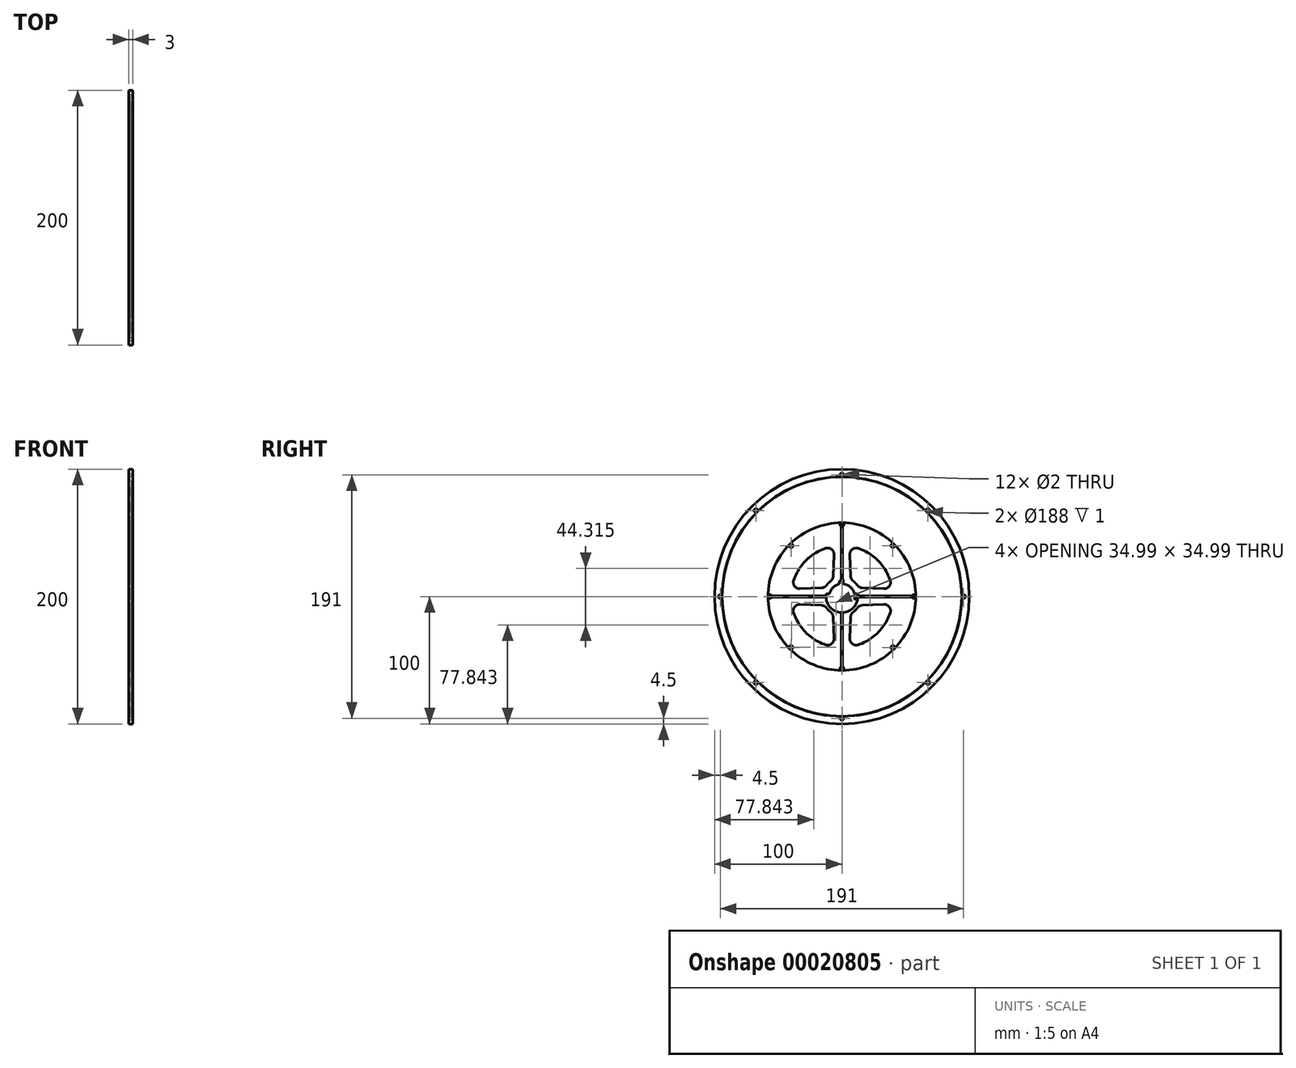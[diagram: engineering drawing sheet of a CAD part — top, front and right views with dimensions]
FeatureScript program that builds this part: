
annotation { "Feature Type Name" : "Feature", "Feature Type Description" : "" }
export const myFeature = defineFeature(function(context is Context, id is Id, definition is map)
    precondition{}
    {
        {
            var Q0;
            Q0=qCreatedBy(makeId("Right.planeOp"),FACE);
            var sketch = newSketch(context, id + "F0", { "sketchPlane" : qUnion([Q0])});
            skCircle(sketch, "E0", {"center": v(0, 0) * mm, "radius": 100 * mm});
            skCircle(sketch, "E1", {"center": v(0, 0) * mm, "radius": 97 * mm});
            skCircle(sketch, "E2", {"center": v(0, 0) * mm, "radius": 58 * mm});
            skCircle(sketch, "E3", {"center": v(0, 0) * mm, "radius": 40 * mm});
            skCircle(sketch, "E4", {"center": v(0, 0) * mm, "radius": 15 * mm});
            skCircle(sketch, "E5", {"center": v(0, 0) * mm, "radius": 10 * mm});
            skCircle(sketch, "E6", {"center": v(0, 0) * mm, "radius": 12.5 * mm});
            skCircle(sketch, "E7", {"center": v(0, 0) * mm, "radius": 55 * mm});
            skCircle(sketch, "E8", {"center": v(0, 0) * mm, "radius": 94 * mm});
            skLineSegment(sketch, "E9", {"start": v(-97, 0) * mm, "end": v(-94, 0) * mm});
            skLineSegment(sketch, "E10", {"start": v(-58, 0) * mm, "end": v(-55, 0) * mm});
            skLineSegment(sketch, "E11.rect.bottom", {"start": v(-55, -0.5) * mm, "end": v(55, -0.5) * mm});
            skLineSegment(sketch, "E11.rect.top", {"start": v(-55, 0.5) * mm, "end": v(55, 0.5) * mm});
            skLineSegment(sketch, "E11.rect.left", {"start": v(-55, -0.5) * mm, "end": v(-55, 0.5) * mm});
            skLineSegment(sketch, "E11.rect.right", {"start": v(55, -0.5) * mm, "end": v(55, 0.5) * mm});
            skEllipse(sketch, "E12", {"center": v(-55, 0) * mm, "majorRadius": 1.5 * mm, "minorRadius": 0.5 * mm, "majorAxis": v(-1, 0)});
            skEllipse(sketch, "E13.1.0", {"center": v(0, -55) * mm, "majorRadius": 1.5 * mm, "minorRadius": 0.5 * mm, "majorAxis": v(0, -1)});
            skEllipse(sketch, "E13.2.0", {"center": v(55, 0) * mm, "majorRadius": 1.5 * mm, "minorRadius": 0.5 * mm, "majorAxis": v(1, 0)});
            skEllipse(sketch, "E13.3.0", {"center": v(0, 55) * mm, "majorRadius": 1.5 * mm, "minorRadius": 0.5 * mm, "majorAxis": v(0, 1)});
            skLineSegment(sketch, "E14.rect.bottom", {"start": v(-0.5, 55) * mm, "end": v(0.5, 55) * mm});
            skLineSegment(sketch, "E14.rect.top", {"start": v(-0.5, -55) * mm, "end": v(0.5, -55) * mm});
            skLineSegment(sketch, "E14.rect.left", {"start": v(-0.5, 55) * mm, "end": v(-0.5, -55) * mm});
            skLineSegment(sketch, "E14.rect.right", {"start": v(0.5, 55) * mm, "end": v(0.5, -55) * mm});
            skCircle(sketch, "E15.cCircle", {"center": v(0, 0) * mm, "radius": 58 * mm, "construction": true});
            skPoint(sketch, "E16.0.midPoint", {"position": v(-58, 0) * mm});
            skLineSegment(sketch, "E17.rect.bottom", {"start": v(-2, 12.34) * mm, "end": v(2, 12.34) * mm});
            skLineSegment(sketch, "E17.rect.top", {"start": v(-2, -12.34) * mm, "end": v(2, -12.34) * mm});
            skLineSegment(sketch, "E17.rect.left", {"start": v(-2, 12.34) * mm, "end": v(-2, -12.34) * mm});
            skLineSegment(sketch, "E17.rect.right", {"start": v(2, 12.34) * mm, "end": v(2, -12.34) * mm});
            skLineSegment(sketch, "E18.rect.bottom", {"start": v(-12.34, -2) * mm, "end": v(12.34, -2) * mm});
            skLineSegment(sketch, "E18.rect.top", {"start": v(-12.34, 2) * mm, "end": v(12.34, 2) * mm});
            skLineSegment(sketch, "E18.rect.left", {"start": v(-12.34, -2) * mm, "end": v(-12.34, 2) * mm});
            skLineSegment(sketch, "E18.rect.right", {"start": v(12.34, -2) * mm, "end": v(12.34, 2) * mm});
            skCircle(sketch, "E19", {"center": v(12.5, 0) * mm, "radius": 0.5 * mm});
            skCircle(sketch, "E20", {"center": v(0, 12.5) * mm, "radius": 0.5 * mm});
            skCircle(sketch, "E21", {"center": v(-12.5, 0) * mm, "radius": 0.5 * mm});
            skCircle(sketch, "E22", {"center": v(0, -12.5) * mm, "radius": 0.5 * mm});
            skPoint(sketch, "E23.0.midPoint", {"position": v(58, 0) * mm});
            skLineSegment(sketch, "E24", {"start": v(5.87, 39.57) * mm, "end": v(7.02, 13.26) * mm});
            skLineSegment(sketch, "E25", {"start": v(-5.87, 39.57) * mm, "end": v(-7.02, 13.26) * mm});
            skLineSegment(sketch, "E26", {"start": v(5.87, -39.57) * mm, "end": v(7.02, -13.26) * mm});
            skLineSegment(sketch, "E27", {"start": v(-5.87, -39.57) * mm, "end": v(-7.02, -13.26) * mm});
            skLineSegment(sketch, "E28", {"start": v(-39.57, -5.87) * mm, "end": v(-13.26, -7.02) * mm});
            skLineSegment(sketch, "E29", {"start": v(-39.57, 5.87) * mm, "end": v(-13.26, 7.02) * mm});
            skLineSegment(sketch, "E30", {"start": v(39.57, 5.87) * mm, "end": v(13.26, 7.02) * mm});
            skLineSegment(sketch, "E31", {"start": v(39.57, -5.87) * mm, "end": v(13.26, -7.02) * mm});
            skSolve(sketch);
        }
        {
            var Q0;
            {var subQ0=sQuery(id+"F0.wireOp",EDGE,"E25");Q0=makeQuery(id+"F0.imprint","IMPRINT",FACE,{"disambiguationData":[TD([[makeQuery(id+"F0.imprint","IMPRINT",EDGE,{"derivedFrom":subQ0}),1.0]])]});}
            var Q1;
            {var subQ0=sQuery(id+"F0.wireOp",EDGE,"E24");Q1=makeQuery(id+"F0.imprint","IMPRINT",FACE,{"disambiguationData":[TD([[makeQuery(id+"F0.imprint","IMPRINT",EDGE,{"derivedFrom":subQ0}),-1.0]])]});}
            var Q2;
            {var subQ0=sQuery(id+"F0.wireOp",EDGE,"E14.rect.right");var subQ3=sQuery(id+"F0.wireOp",EDGE,"E3");var subQ4=makeQuery(id+"F0.imprint","INTERSECT",VERTEX,{"disambiguationData":[OD(0.0)],"derivedFrom":[subQ3,subQ0]});Q2=makeQuery(id+"F0.imprint","IMPRINT",FACE,{"disambiguationData":[TD([[makeQuery(id+"F0.imprint","IMPRINT",EDGE,{"disambiguationData":[TD([[subQ4,-1.0]])],"derivedFrom":subQ3}),1.0]])]});}
            var Q3;
            {var subQ1=sQuery(id+"F0.wireOp",EDGE,"E3");var subQ9=makeQuery(id+"F0.imprint","INTERSECT",VERTEX,{"derivedFrom":[subQ1,sQuery(id+"F0.wireOp",EDGE,"E25")]});Q3=makeQuery(id+"F0.imprint","IMPRINT",FACE,{"disambiguationData":[TD([[makeQuery(id+"F0.imprint","IMPRINT",EDGE,{"disambiguationData":[TD([[subQ9,1.0]])],"derivedFrom":subQ1}),-1.0]])]});}
            var Q4;
            {var subQ1=sQuery(id+"F0.wireOp",EDGE,"E3");var subQ8=makeQuery(id+"F0.imprint","INTERSECT",VERTEX,{"derivedFrom":[subQ1,sQuery(id+"F0.wireOp",EDGE,"E30")]});Q4=makeQuery(id+"F0.imprint","IMPRINT",FACE,{"disambiguationData":[TD([[makeQuery(id+"F0.imprint","IMPRINT",EDGE,{"disambiguationData":[TD([[subQ8,1.0]])],"derivedFrom":subQ1}),-1.0]])]});}
            var Q5;
            {var subQ0=sQuery(id+"F0.wireOp",EDGE,"E14.rect.right");var subQ1=sQuery(id+"F0.wireOp",EDGE,"E3");var subQ2=makeQuery(id+"F0.imprint","INTERSECT",VERTEX,{"disambiguationData":[OD(0.0)],"derivedFrom":[subQ1,subQ0]});Q5=makeQuery(id+"F0.imprint","IMPRINT",FACE,{"disambiguationData":[TD([[makeQuery(id+"F0.imprint","IMPRINT",EDGE,{"disambiguationData":[TD([[subQ2,-1.0]])],"derivedFrom":subQ1}),-1.0]])]});}
            var Q6;
            Q6=makeQuery(id+"F0.imprint","IMPRINT",FACE,{"disambiguationData":[TD([[makeQuery(id+"F0.imprint","IMPRINT",EDGE,{"derivedFrom":sQuery(id+"F0.wireOp",EDGE,"E2")}),1.0]])]});
            var Q7;
            {var subQ1=sQuery(id+"F0.wireOp",EDGE,"E3");var subQ9=makeQuery(id+"F0.imprint","INTERSECT",VERTEX,{"derivedFrom":[subQ1,sQuery(id+"F0.wireOp",EDGE,"E28")]});Q7=makeQuery(id+"F0.imprint","IMPRINT",FACE,{"disambiguationData":[TD([[makeQuery(id+"F0.imprint","IMPRINT",EDGE,{"disambiguationData":[TD([[subQ9,1.0]])],"derivedFrom":subQ1}),-1.0]])]});}
            var Q8;
            {var subQ0=sQuery(id+"F0.wireOp",EDGE,"E29");Q8=makeQuery(id+"F0.imprint","IMPRINT",FACE,{"disambiguationData":[TD([[makeQuery(id+"F0.imprint","IMPRINT",EDGE,{"derivedFrom":subQ0}),-1.0]])]});}
            var Q9;
            {var subQ0=sQuery(id+"F0.wireOp",EDGE,"E28");Q9=makeQuery(id+"F0.imprint","IMPRINT",FACE,{"disambiguationData":[TD([[makeQuery(id+"F0.imprint","IMPRINT",EDGE,{"derivedFrom":subQ0}),1.0]])]});}
            var Q10;
            {var subQ4=sQuery(id+"F0.wireOp",EDGE,"E4");var subQ13=makeQuery(id+"F0.imprint","INTERSECT",VERTEX,{"derivedFrom":[subQ4,sQuery(id+"F0.wireOp",EDGE,"E25")]});Q10=makeQuery(id+"F0.imprint","IMPRINT",FACE,{"disambiguationData":[TD([[makeQuery(id+"F0.imprint","IMPRINT",EDGE,{"disambiguationData":[TD([[subQ13,1.0]])],"derivedFrom":subQ4}),1.0]])]});}
            var Q11;
            {var subQ1=sQuery(id+"F0.wireOp",EDGE,"E5");var subQ5=sQuery(id+"F0.wireOp",EDGE,"E17.rect.left");var subQ6=makeQuery(id+"F0.imprint","INTERSECT",VERTEX,{"disambiguationData":[OD(0.0)],"derivedFrom":[subQ1,subQ5]});Q11=makeQuery(id+"F0.imprint","IMPRINT",FACE,{"disambiguationData":[TD([[makeQuery(id+"F0.imprint","IMPRINT",EDGE,{"disambiguationData":[TD([[subQ6,-1.0]])],"derivedFrom":subQ1}),-1.0]])]});}
            var Q12;
            {var subQ2=sQuery(id+"F0.wireOp",EDGE,"E4");var subQ13=makeQuery(id+"F0.imprint","INTERSECT",VERTEX,{"derivedFrom":[subQ2,sQuery(id+"F0.wireOp",EDGE,"E28")]});Q12=makeQuery(id+"F0.imprint","IMPRINT",FACE,{"disambiguationData":[TD([[makeQuery(id+"F0.imprint","IMPRINT",EDGE,{"disambiguationData":[TD([[subQ13,1.0]])],"derivedFrom":subQ2}),1.0]])]});}
            var Q13;
            {var subQ0=sQuery(id+"F0.wireOp",EDGE,"E18.rect.bottom");var subQ1=sQuery(id+"F0.wireOp",EDGE,"E5");var subQ2=makeQuery(id+"F0.imprint","INTERSECT",VERTEX,{"disambiguationData":[OD(0.0)],"derivedFrom":[subQ1,subQ0]});Q13=makeQuery(id+"F0.imprint","IMPRINT",FACE,{"disambiguationData":[TD([[makeQuery(id+"F0.imprint","IMPRINT",EDGE,{"disambiguationData":[TD([[subQ2,-1.0]])],"derivedFrom":subQ1}),-1.0]])]});}
            var Q14;
            {var subQ0=sQuery(id+"F0.wireOp",EDGE,"E18.rect.top");var subQ1=sQuery(id+"F0.wireOp",EDGE,"E5");var subQ2=makeQuery(id+"F0.imprint","INTERSECT",VERTEX,{"disambiguationData":[OD(0.0)],"derivedFrom":[subQ1,subQ0]});Q14=makeQuery(id+"F0.imprint","IMPRINT",FACE,{"disambiguationData":[TD([[makeQuery(id+"F0.imprint","IMPRINT",EDGE,{"disambiguationData":[TD([[subQ2,-1.0]])],"derivedFrom":subQ1}),-1.0]])]});}
            var Q15;
            {var subQ6=sQuery(id+"F0.wireOp",EDGE,"E4");var subQ13=makeQuery(id+"F0.imprint","INTERSECT",VERTEX,{"derivedFrom":[subQ6,sQuery(id+"F0.wireOp",EDGE,"E30")]});Q15=makeQuery(id+"F0.imprint","IMPRINT",FACE,{"disambiguationData":[TD([[makeQuery(id+"F0.imprint","IMPRINT",EDGE,{"disambiguationData":[TD([[subQ13,1.0]])],"derivedFrom":subQ6}),1.0]])]});}
            var Q16;
            {var subQ0=sQuery(id+"F0.wireOp",EDGE,"E30");Q16=makeQuery(id+"F0.imprint","IMPRINT",FACE,{"disambiguationData":[TD([[makeQuery(id+"F0.imprint","IMPRINT",EDGE,{"derivedFrom":subQ0}),1.0]])]});}
            var Q17;
            {var subQ0=sQuery(id+"F0.wireOp",EDGE,"E31");Q17=makeQuery(id+"F0.imprint","IMPRINT",FACE,{"disambiguationData":[TD([[makeQuery(id+"F0.imprint","IMPRINT",EDGE,{"derivedFrom":subQ0}),-1.0]])]});}
            var Q18;
            {var subQ1=sQuery(id+"F0.wireOp",EDGE,"E3");var subQ9=makeQuery(id+"F0.imprint","INTERSECT",VERTEX,{"derivedFrom":[subQ1,sQuery(id+"F0.wireOp",EDGE,"E26")]});Q18=makeQuery(id+"F0.imprint","IMPRINT",FACE,{"disambiguationData":[TD([[makeQuery(id+"F0.imprint","IMPRINT",EDGE,{"disambiguationData":[TD([[subQ9,1.0]])],"derivedFrom":subQ1}),-1.0]])]});}
            var Q19;
            {var subQ2=sQuery(id+"F0.wireOp",EDGE,"E11.rect.top");var subQ7=sQuery(id+"F0.wireOp",EDGE,"E3");var subQ8=makeQuery(id+"F0.imprint","INTERSECT",VERTEX,{"disambiguationData":[OD(0.0)],"derivedFrom":[subQ7,subQ2]});Q19=makeQuery(id+"F0.imprint","IMPRINT",FACE,{"disambiguationData":[TD([[makeQuery(id+"F0.imprint","IMPRINT",EDGE,{"disambiguationData":[TD([[subQ8,1.0]])],"derivedFrom":subQ7}),-1.0]])]});}
            var Q20;
            {var subQ0=sQuery(id+"F0.wireOp",EDGE,"E11.rect.top");var subQ3=sQuery(id+"F0.wireOp",EDGE,"E3");var subQ4=makeQuery(id+"F0.imprint","INTERSECT",VERTEX,{"disambiguationData":[OD(0.0)],"derivedFrom":[subQ3,subQ0]});Q20=makeQuery(id+"F0.imprint","IMPRINT",FACE,{"disambiguationData":[TD([[makeQuery(id+"F0.imprint","IMPRINT",EDGE,{"disambiguationData":[TD([[subQ4,1.0]])],"derivedFrom":subQ3}),1.0]])]});}
            var Q21;
            {var subQ1=sQuery(id+"F0.wireOp",EDGE,"E11.rect.top");var subQ5=sQuery(id+"F0.wireOp",EDGE,"E4");var subQ6=makeQuery(id+"F0.imprint","INTERSECT",VERTEX,{"disambiguationData":[OD(0.0)],"derivedFrom":[subQ5,subQ1]});Q21=makeQuery(id+"F0.imprint","IMPRINT",FACE,{"disambiguationData":[TD([[makeQuery(id+"F0.imprint","IMPRINT",EDGE,{"disambiguationData":[TD([[subQ6,1.0]])],"derivedFrom":subQ5}),1.0]])]});}
            var Q22;
            {var subQ2=sQuery(id+"F0.wireOp",EDGE,"E4");var subQ13=makeQuery(id+"F0.imprint","INTERSECT",VERTEX,{"derivedFrom":[subQ2,sQuery(id+"F0.wireOp",EDGE,"E26")]});Q22=makeQuery(id+"F0.imprint","IMPRINT",FACE,{"disambiguationData":[TD([[makeQuery(id+"F0.imprint","IMPRINT",EDGE,{"disambiguationData":[TD([[subQ13,1.0]])],"derivedFrom":subQ2}),1.0]])]});}
            var Q23;
            {var subQ1=sQuery(id+"F0.wireOp",EDGE,"E5");var subQ5=sQuery(id+"F0.wireOp",EDGE,"E17.rect.right");var subQ6=makeQuery(id+"F0.imprint","INTERSECT",VERTEX,{"disambiguationData":[OD(1.0)],"derivedFrom":[subQ1,subQ5]});Q23=makeQuery(id+"F0.imprint","IMPRINT",FACE,{"disambiguationData":[TD([[makeQuery(id+"F0.imprint","IMPRINT",EDGE,{"disambiguationData":[TD([[subQ6,-1.0]])],"derivedFrom":subQ1}),-1.0]])]});}
            var Q24;
            {var subQ0=sQuery(id+"F0.wireOp",EDGE,"E11.rect.top");var subQ3=sQuery(id+"F0.wireOp",EDGE,"E3");var subQ4=makeQuery(id+"F0.imprint","INTERSECT",VERTEX,{"disambiguationData":[OD(1.0)],"derivedFrom":[subQ3,subQ0]});Q24=makeQuery(id+"F0.imprint","IMPRINT",FACE,{"disambiguationData":[TD([[makeQuery(id+"F0.imprint","IMPRINT",EDGE,{"disambiguationData":[TD([[subQ4,-1.0]])],"derivedFrom":subQ3}),1.0]])]});}
            var Q25;
            {var subQ1=sQuery(id+"F0.wireOp",EDGE,"E11.rect.top");var subQ5=sQuery(id+"F0.wireOp",EDGE,"E4");var subQ6=makeQuery(id+"F0.imprint","INTERSECT",VERTEX,{"disambiguationData":[OD(1.0)],"derivedFrom":[subQ5,subQ1]});Q25=makeQuery(id+"F0.imprint","IMPRINT",FACE,{"disambiguationData":[TD([[makeQuery(id+"F0.imprint","IMPRINT",EDGE,{"disambiguationData":[TD([[subQ6,-1.0]])],"derivedFrom":subQ5}),1.0]])]});}
            var Q26;
            {var subQ2=sQuery(id+"F0.wireOp",EDGE,"E11.rect.top");var subQ7=sQuery(id+"F0.wireOp",EDGE,"E3");var subQ8=makeQuery(id+"F0.imprint","INTERSECT",VERTEX,{"disambiguationData":[OD(1.0)],"derivedFrom":[subQ7,subQ2]});Q26=makeQuery(id+"F0.imprint","IMPRINT",FACE,{"disambiguationData":[TD([[makeQuery(id+"F0.imprint","IMPRINT",EDGE,{"disambiguationData":[TD([[subQ8,-1.0]])],"derivedFrom":subQ7}),-1.0]])]});}
            var Q27;
            {var subQ1=sQuery(id+"F0.wireOp",EDGE,"E14.rect.right");var subQ5=sQuery(id+"F0.wireOp",EDGE,"E4");var subQ6=makeQuery(id+"F0.imprint","INTERSECT",VERTEX,{"disambiguationData":[OD(0.0)],"derivedFrom":[subQ5,subQ1]});Q27=makeQuery(id+"F0.imprint","IMPRINT",FACE,{"disambiguationData":[TD([[makeQuery(id+"F0.imprint","IMPRINT",EDGE,{"disambiguationData":[TD([[subQ6,-1.0]])],"derivedFrom":subQ5}),1.0]])]});}
            var Q28;
            {var subQ0=sQuery(id+"F0.wireOp",EDGE,"E27");Q28=makeQuery(id+"F0.imprint","IMPRINT",FACE,{"disambiguationData":[TD([[makeQuery(id+"F0.imprint","IMPRINT",EDGE,{"derivedFrom":subQ0}),-1.0]])]});}
            var Q29;
            {var subQ0=sQuery(id+"F0.wireOp",EDGE,"E26");Q29=makeQuery(id+"F0.imprint","IMPRINT",FACE,{"disambiguationData":[TD([[makeQuery(id+"F0.imprint","IMPRINT",EDGE,{"derivedFrom":subQ0}),1.0]])]});}
            var Q30;
            {var subQ3=sQuery(id+"F0.wireOp",EDGE,"E3");var subQ5=sQuery(id+"F0.wireOp",EDGE,"E14.rect.left");var subQ7=makeQuery(id+"F0.imprint","INTERSECT",VERTEX,{"disambiguationData":[OD(1.0)],"derivedFrom":[subQ3,subQ5]});Q30=makeQuery(id+"F0.imprint","IMPRINT",FACE,{"disambiguationData":[TD([[makeQuery(id+"F0.imprint","IMPRINT",EDGE,{"disambiguationData":[TD([[subQ7,-1.0]])],"derivedFrom":subQ3}),1.0]])]});}
            var Q31;
            {var subQ0=sQuery(id+"F0.wireOp",EDGE,"E14.rect.left");var subQ1=sQuery(id+"F0.wireOp",EDGE,"E3");var subQ2=makeQuery(id+"F0.imprint","INTERSECT",VERTEX,{"disambiguationData":[OD(1.0)],"derivedFrom":[subQ1,subQ0]});Q31=makeQuery(id+"F0.imprint","IMPRINT",FACE,{"disambiguationData":[TD([[makeQuery(id+"F0.imprint","IMPRINT",EDGE,{"disambiguationData":[TD([[subQ2,-1.0]])],"derivedFrom":subQ1}),-1.0]])]});}
            var Q32;
            {var subQ3=sQuery(id+"F0.wireOp",EDGE,"E14.rect.left");var subQ5=sQuery(id+"F0.wireOp",EDGE,"E4");var subQ7=makeQuery(id+"F0.imprint","INTERSECT",VERTEX,{"disambiguationData":[OD(1.0)],"derivedFrom":[subQ5,subQ3]});Q32=makeQuery(id+"F0.imprint","IMPRINT",FACE,{"disambiguationData":[TD([[makeQuery(id+"F0.imprint","IMPRINT",EDGE,{"disambiguationData":[TD([[subQ7,-1.0]])],"derivedFrom":subQ5}),1.0]])]});}
            var Q33;
            Q33=makeQuery(id+"F0.imprint","IMPRINT",FACE,{"disambiguationData":[TD([[makeQuery(id+"F0.imprint","IMPRINT",EDGE,{"derivedFrom":sQuery(id+"F0.wireOp",EDGE,"E1")}),1.0]])]});
            var Q34;
            Q34=makeQuery(id+"F0.imprint","IMPRINT",FACE,{"disambiguationData":[TD([[makeQuery(id+"F0.imprint","IMPRINT",EDGE,{"derivedFrom":sQuery(id+"F0.wireOp",EDGE,"E0")}),1.0]])]});
            extrude(context, id + "F1", {"entities" : qUnion([Q0, Q1, Q2, Q3, Q4, Q5, Q6, Q7, Q8, Q9, Q10, Q11, Q12, Q13, Q14, Q15, Q16, Q17, Q18, Q19, Q20, Q21, Q22, Q23, Q24, Q25, Q26, Q27, Q28, Q29, Q30, Q31, Q32, Q33, Q34]), "oppositeDirection" : true, "depth" : 1 * mm});
        }
        {
            var Q0;
            {var subQ1=sQuery(id+"F0.wireOp",EDGE,"E3");var subQ9=makeQuery(id+"F0.imprint","INTERSECT",VERTEX,{"derivedFrom":[subQ1,sQuery(id+"F0.wireOp",EDGE,"E28")]});Q0=makeQuery(id+"F0.imprint","IMPRINT",FACE,{"disambiguationData":[TD([[makeQuery(id+"F0.imprint","IMPRINT",EDGE,{"disambiguationData":[TD([[subQ9,1.0]])],"derivedFrom":subQ1}),-1.0]])]});}
            var Q1;
            Q1=makeQuery(id+"F0.imprint","IMPRINT",FACE,{"disambiguationData":[TD([[makeQuery(id+"F0.imprint","IMPRINT",EDGE,{"derivedFrom":sQuery(id+"F0.wireOp",EDGE,"E2")}),1.0]])]});
            var Q2;
            {var subQ0=sQuery(id+"F0.wireOp",EDGE,"E28");Q2=makeQuery(id+"F0.imprint","IMPRINT",FACE,{"disambiguationData":[TD([[makeQuery(id+"F0.imprint","IMPRINT",EDGE,{"derivedFrom":subQ0}),1.0]])]});}
            var Q3;
            {var subQ0=sQuery(id+"F0.wireOp",EDGE,"E29");Q3=makeQuery(id+"F0.imprint","IMPRINT",FACE,{"disambiguationData":[TD([[makeQuery(id+"F0.imprint","IMPRINT",EDGE,{"derivedFrom":subQ0}),-1.0]])]});}
            var Q4;
            {var subQ1=sQuery(id+"F0.wireOp",EDGE,"E3");var subQ9=makeQuery(id+"F0.imprint","INTERSECT",VERTEX,{"derivedFrom":[subQ1,sQuery(id+"F0.wireOp",EDGE,"E25")]});Q4=makeQuery(id+"F0.imprint","IMPRINT",FACE,{"disambiguationData":[TD([[makeQuery(id+"F0.imprint","IMPRINT",EDGE,{"disambiguationData":[TD([[subQ9,1.0]])],"derivedFrom":subQ1}),-1.0]])]});}
            var Q5;
            {var subQ2=sQuery(id+"F0.wireOp",EDGE,"E11.rect.top");var subQ7=sQuery(id+"F0.wireOp",EDGE,"E3");var subQ8=makeQuery(id+"F0.imprint","INTERSECT",VERTEX,{"disambiguationData":[OD(1.0)],"derivedFrom":[subQ7,subQ2]});Q5=makeQuery(id+"F0.imprint","IMPRINT",FACE,{"disambiguationData":[TD([[makeQuery(id+"F0.imprint","IMPRINT",EDGE,{"disambiguationData":[TD([[subQ8,-1.0]])],"derivedFrom":subQ7}),-1.0]])]});}
            var Q6;
            {var subQ0=sQuery(id+"F0.wireOp",EDGE,"E27");Q6=makeQuery(id+"F0.imprint","IMPRINT",FACE,{"disambiguationData":[TD([[makeQuery(id+"F0.imprint","IMPRINT",EDGE,{"derivedFrom":subQ0}),-1.0]])]});}
            var Q7;
            {var subQ0=sQuery(id+"F0.wireOp",EDGE,"E26");Q7=makeQuery(id+"F0.imprint","IMPRINT",FACE,{"disambiguationData":[TD([[makeQuery(id+"F0.imprint","IMPRINT",EDGE,{"derivedFrom":subQ0}),1.0]])]});}
            var Q8;
            {var subQ3=sQuery(id+"F0.wireOp",EDGE,"E3");var subQ5=sQuery(id+"F0.wireOp",EDGE,"E14.rect.left");var subQ7=makeQuery(id+"F0.imprint","INTERSECT",VERTEX,{"disambiguationData":[OD(1.0)],"derivedFrom":[subQ3,subQ5]});Q8=makeQuery(id+"F0.imprint","IMPRINT",FACE,{"disambiguationData":[TD([[makeQuery(id+"F0.imprint","IMPRINT",EDGE,{"disambiguationData":[TD([[subQ7,-1.0]])],"derivedFrom":subQ3}),1.0]])]});}
            var Q9;
            {var subQ2=sQuery(id+"F0.wireOp",EDGE,"E4");var subQ13=makeQuery(id+"F0.imprint","INTERSECT",VERTEX,{"derivedFrom":[subQ2,sQuery(id+"F0.wireOp",EDGE,"E26")]});Q9=makeQuery(id+"F0.imprint","IMPRINT",FACE,{"disambiguationData":[TD([[makeQuery(id+"F0.imprint","IMPRINT",EDGE,{"disambiguationData":[TD([[subQ13,1.0]])],"derivedFrom":subQ2}),1.0]])]});}
            var Q10;
            {var subQ1=sQuery(id+"F0.wireOp",EDGE,"E5");var subQ5=sQuery(id+"F0.wireOp",EDGE,"E17.rect.right");var subQ6=makeQuery(id+"F0.imprint","INTERSECT",VERTEX,{"disambiguationData":[OD(1.0)],"derivedFrom":[subQ1,subQ5]});Q10=makeQuery(id+"F0.imprint","IMPRINT",FACE,{"disambiguationData":[TD([[makeQuery(id+"F0.imprint","IMPRINT",EDGE,{"disambiguationData":[TD([[subQ6,-1.0]])],"derivedFrom":subQ1}),-1.0]])]});}
            var Q11;
            {var subQ0=sQuery(id+"F0.wireOp",EDGE,"E18.rect.bottom");var subQ1=sQuery(id+"F0.wireOp",EDGE,"E5");var subQ2=makeQuery(id+"F0.imprint","INTERSECT",VERTEX,{"disambiguationData":[OD(0.0)],"derivedFrom":[subQ1,subQ0]});Q11=makeQuery(id+"F0.imprint","IMPRINT",FACE,{"disambiguationData":[TD([[makeQuery(id+"F0.imprint","IMPRINT",EDGE,{"disambiguationData":[TD([[subQ2,-1.0]])],"derivedFrom":subQ1}),-1.0]])]});}
            var Q12;
            {var subQ2=sQuery(id+"F0.wireOp",EDGE,"E4");var subQ13=makeQuery(id+"F0.imprint","INTERSECT",VERTEX,{"derivedFrom":[subQ2,sQuery(id+"F0.wireOp",EDGE,"E28")]});Q12=makeQuery(id+"F0.imprint","IMPRINT",FACE,{"disambiguationData":[TD([[makeQuery(id+"F0.imprint","IMPRINT",EDGE,{"disambiguationData":[TD([[subQ13,1.0]])],"derivedFrom":subQ2}),1.0]])]});}
            var Q13;
            {var subQ3=sQuery(id+"F0.wireOp",EDGE,"E14.rect.left");var subQ5=sQuery(id+"F0.wireOp",EDGE,"E4");var subQ7=makeQuery(id+"F0.imprint","INTERSECT",VERTEX,{"disambiguationData":[OD(1.0)],"derivedFrom":[subQ5,subQ3]});Q13=makeQuery(id+"F0.imprint","IMPRINT",FACE,{"disambiguationData":[TD([[makeQuery(id+"F0.imprint","IMPRINT",EDGE,{"disambiguationData":[TD([[subQ7,-1.0]])],"derivedFrom":subQ5}),1.0]])]});}
            var Q14;
            {var subQ6=sQuery(id+"F0.wireOp",EDGE,"E4");var subQ13=makeQuery(id+"F0.imprint","INTERSECT",VERTEX,{"derivedFrom":[subQ6,sQuery(id+"F0.wireOp",EDGE,"E30")]});Q14=makeQuery(id+"F0.imprint","IMPRINT",FACE,{"disambiguationData":[TD([[makeQuery(id+"F0.imprint","IMPRINT",EDGE,{"disambiguationData":[TD([[subQ13,1.0]])],"derivedFrom":subQ6}),1.0]])]});}
            var Q15;
            {var subQ0=sQuery(id+"F0.wireOp",EDGE,"E30");Q15=makeQuery(id+"F0.imprint","IMPRINT",FACE,{"disambiguationData":[TD([[makeQuery(id+"F0.imprint","IMPRINT",EDGE,{"derivedFrom":subQ0}),1.0]])]});}
            var Q16;
            {var subQ0=sQuery(id+"F0.wireOp",EDGE,"E31");Q16=makeQuery(id+"F0.imprint","IMPRINT",FACE,{"disambiguationData":[TD([[makeQuery(id+"F0.imprint","IMPRINT",EDGE,{"derivedFrom":subQ0}),-1.0]])]});}
            var Q17;
            {var subQ1=sQuery(id+"F0.wireOp",EDGE,"E11.rect.top");var subQ5=sQuery(id+"F0.wireOp",EDGE,"E4");var subQ6=makeQuery(id+"F0.imprint","INTERSECT",VERTEX,{"disambiguationData":[OD(0.0)],"derivedFrom":[subQ5,subQ1]});Q17=makeQuery(id+"F0.imprint","IMPRINT",FACE,{"disambiguationData":[TD([[makeQuery(id+"F0.imprint","IMPRINT",EDGE,{"disambiguationData":[TD([[subQ6,1.0]])],"derivedFrom":subQ5}),1.0]])]});}
            var Q18;
            {var subQ0=sQuery(id+"F0.wireOp",EDGE,"E11.rect.top");var subQ3=sQuery(id+"F0.wireOp",EDGE,"E3");var subQ4=makeQuery(id+"F0.imprint","INTERSECT",VERTEX,{"disambiguationData":[OD(0.0)],"derivedFrom":[subQ3,subQ0]});Q18=makeQuery(id+"F0.imprint","IMPRINT",FACE,{"disambiguationData":[TD([[makeQuery(id+"F0.imprint","IMPRINT",EDGE,{"disambiguationData":[TD([[subQ4,1.0]])],"derivedFrom":subQ3}),1.0]])]});}
            var Q19;
            {var subQ0=sQuery(id+"F0.wireOp",EDGE,"E11.rect.top");var subQ3=sQuery(id+"F0.wireOp",EDGE,"E3");var subQ4=makeQuery(id+"F0.imprint","INTERSECT",VERTEX,{"disambiguationData":[OD(1.0)],"derivedFrom":[subQ3,subQ0]});Q19=makeQuery(id+"F0.imprint","IMPRINT",FACE,{"disambiguationData":[TD([[makeQuery(id+"F0.imprint","IMPRINT",EDGE,{"disambiguationData":[TD([[subQ4,-1.0]])],"derivedFrom":subQ3}),1.0]])]});}
            var Q20;
            {var subQ1=sQuery(id+"F0.wireOp",EDGE,"E11.rect.top");var subQ5=sQuery(id+"F0.wireOp",EDGE,"E4");var subQ6=makeQuery(id+"F0.imprint","INTERSECT",VERTEX,{"disambiguationData":[OD(1.0)],"derivedFrom":[subQ5,subQ1]});Q20=makeQuery(id+"F0.imprint","IMPRINT",FACE,{"disambiguationData":[TD([[makeQuery(id+"F0.imprint","IMPRINT",EDGE,{"disambiguationData":[TD([[subQ6,-1.0]])],"derivedFrom":subQ5}),1.0]])]});}
            var Q21;
            {var subQ4=sQuery(id+"F0.wireOp",EDGE,"E4");var subQ13=makeQuery(id+"F0.imprint","INTERSECT",VERTEX,{"derivedFrom":[subQ4,sQuery(id+"F0.wireOp",EDGE,"E25")]});Q21=makeQuery(id+"F0.imprint","IMPRINT",FACE,{"disambiguationData":[TD([[makeQuery(id+"F0.imprint","IMPRINT",EDGE,{"disambiguationData":[TD([[subQ13,1.0]])],"derivedFrom":subQ4}),1.0]])]});}
            var Q22;
            {var subQ1=sQuery(id+"F0.wireOp",EDGE,"E5");var subQ5=sQuery(id+"F0.wireOp",EDGE,"E17.rect.left");var subQ6=makeQuery(id+"F0.imprint","INTERSECT",VERTEX,{"disambiguationData":[OD(0.0)],"derivedFrom":[subQ1,subQ5]});Q22=makeQuery(id+"F0.imprint","IMPRINT",FACE,{"disambiguationData":[TD([[makeQuery(id+"F0.imprint","IMPRINT",EDGE,{"disambiguationData":[TD([[subQ6,-1.0]])],"derivedFrom":subQ1}),-1.0]])]});}
            var Q23;
            {var subQ1=sQuery(id+"F0.wireOp",EDGE,"E3");var subQ9=makeQuery(id+"F0.imprint","INTERSECT",VERTEX,{"derivedFrom":[subQ1,sQuery(id+"F0.wireOp",EDGE,"E26")]});Q23=makeQuery(id+"F0.imprint","IMPRINT",FACE,{"disambiguationData":[TD([[makeQuery(id+"F0.imprint","IMPRINT",EDGE,{"disambiguationData":[TD([[subQ9,1.0]])],"derivedFrom":subQ1}),-1.0]])]});}
            var Q24;
            {var subQ0=sQuery(id+"F0.wireOp",EDGE,"E14.rect.left");var subQ1=sQuery(id+"F0.wireOp",EDGE,"E3");var subQ2=makeQuery(id+"F0.imprint","INTERSECT",VERTEX,{"disambiguationData":[OD(1.0)],"derivedFrom":[subQ1,subQ0]});Q24=makeQuery(id+"F0.imprint","IMPRINT",FACE,{"disambiguationData":[TD([[makeQuery(id+"F0.imprint","IMPRINT",EDGE,{"disambiguationData":[TD([[subQ2,-1.0]])],"derivedFrom":subQ1}),-1.0]])]});}
            var Q25;
            {var subQ1=sQuery(id+"F0.wireOp",EDGE,"E3");var subQ8=makeQuery(id+"F0.imprint","INTERSECT",VERTEX,{"derivedFrom":[subQ1,sQuery(id+"F0.wireOp",EDGE,"E30")]});Q25=makeQuery(id+"F0.imprint","IMPRINT",FACE,{"disambiguationData":[TD([[makeQuery(id+"F0.imprint","IMPRINT",EDGE,{"disambiguationData":[TD([[subQ8,1.0]])],"derivedFrom":subQ1}),-1.0]])]});}
            var Q26;
            {var subQ2=sQuery(id+"F0.wireOp",EDGE,"E11.rect.top");var subQ7=sQuery(id+"F0.wireOp",EDGE,"E3");var subQ8=makeQuery(id+"F0.imprint","INTERSECT",VERTEX,{"disambiguationData":[OD(0.0)],"derivedFrom":[subQ7,subQ2]});Q26=makeQuery(id+"F0.imprint","IMPRINT",FACE,{"disambiguationData":[TD([[makeQuery(id+"F0.imprint","IMPRINT",EDGE,{"disambiguationData":[TD([[subQ8,1.0]])],"derivedFrom":subQ7}),-1.0]])]});}
            var Q27;
            {var subQ0=sQuery(id+"F0.wireOp",EDGE,"E18.rect.top");var subQ1=sQuery(id+"F0.wireOp",EDGE,"E5");var subQ2=makeQuery(id+"F0.imprint","INTERSECT",VERTEX,{"disambiguationData":[OD(0.0)],"derivedFrom":[subQ1,subQ0]});Q27=makeQuery(id+"F0.imprint","IMPRINT",FACE,{"disambiguationData":[TD([[makeQuery(id+"F0.imprint","IMPRINT",EDGE,{"disambiguationData":[TD([[subQ2,-1.0]])],"derivedFrom":subQ1}),-1.0]])]});}
            var Q28;
            Q28=makeQuery(id+"F0.imprint","IMPRINT",FACE,{"disambiguationData":[TD([[makeQuery(id+"F0.imprint","IMPRINT",EDGE,{"derivedFrom":sQuery(id+"F0.wireOp",EDGE,"E2")}),-1.0]])]});
            var Q29;
            {var subQ0=sQuery(id+"F0.wireOp",EDGE,"E24");Q29=makeQuery(id+"F0.imprint","IMPRINT",FACE,{"disambiguationData":[TD([[makeQuery(id+"F0.imprint","IMPRINT",EDGE,{"derivedFrom":subQ0}),-1.0]])]});}
            var Q30;
            {var subQ0=sQuery(id+"F0.wireOp",EDGE,"E25");Q30=makeQuery(id+"F0.imprint","IMPRINT",FACE,{"disambiguationData":[TD([[makeQuery(id+"F0.imprint","IMPRINT",EDGE,{"derivedFrom":subQ0}),1.0]])]});}
            var Q31;
            {var subQ0=sQuery(id+"F0.wireOp",EDGE,"E14.rect.right");var subQ3=sQuery(id+"F0.wireOp",EDGE,"E3");var subQ4=makeQuery(id+"F0.imprint","INTERSECT",VERTEX,{"disambiguationData":[OD(0.0)],"derivedFrom":[subQ3,subQ0]});Q31=makeQuery(id+"F0.imprint","IMPRINT",FACE,{"disambiguationData":[TD([[makeQuery(id+"F0.imprint","IMPRINT",EDGE,{"disambiguationData":[TD([[subQ4,-1.0]])],"derivedFrom":subQ3}),1.0]])]});}
            var Q32;
            Q32=makeQuery(id+"F0.imprint","IMPRINT",FACE,{"disambiguationData":[TD([[makeQuery(id+"F0.imprint","IMPRINT",EDGE,{"derivedFrom":sQuery(id+"F0.wireOp",EDGE,"E1")}),1.0]])]});
            var Q33;
            Q33=makeQuery(id+"F0.imprint","IMPRINT",FACE,{"disambiguationData":[TD([[makeQuery(id+"F0.imprint","IMPRINT",EDGE,{"derivedFrom":sQuery(id+"F0.wireOp",EDGE,"E0")}),1.0]])]});
            var Q34;
            {var subQ0=sQuery(id+"F0.wireOp",EDGE,"E14.rect.right");var subQ1=sQuery(id+"F0.wireOp",EDGE,"E3");var subQ2=makeQuery(id+"F0.imprint","INTERSECT",VERTEX,{"disambiguationData":[OD(0.0)],"derivedFrom":[subQ1,subQ0]});Q34=makeQuery(id+"F0.imprint","IMPRINT",FACE,{"disambiguationData":[TD([[makeQuery(id+"F0.imprint","IMPRINT",EDGE,{"disambiguationData":[TD([[subQ2,-1.0]])],"derivedFrom":subQ1}),-1.0]])]});}
            extrude(context, id + "F2", {"entities" : qUnion([Q0, Q1, Q2, Q3, Q4, Q5, Q6, Q7, Q8, Q9, Q10, Q11, Q12, Q13, Q14, Q15, Q16, Q17, Q18, Q19, Q20, Q21, Q22, Q23, Q24, Q25, Q26, Q27, Q28, Q29, Q30, Q31, Q32, Q33, Q34]), "operationType" : NewBodyOperationType.ADD, "depth" : 1 * mm});
        }
        {
            var Q0;
            Q0 = qSketchRegion(id + "F0", true);
            var Q1;
            Q1=makeQuery(id+"F0.imprint","IMPRINT",FACE,{"disambiguationData":[TD([[makeQuery(id+"F0.imprint","IMPRINT",EDGE,{"derivedFrom":sQuery(id+"F0.wireOp",EDGE,"E1")}),1.0]])]});
            var Q2;
            {var subQ1=sQuery(id+"F0.wireOp",EDGE,"E3");var subQ9=makeQuery(id+"F0.imprint","INTERSECT",VERTEX,{"derivedFrom":[subQ1,sQuery(id+"F0.wireOp",EDGE,"E25")]});Q2=makeQuery(id+"F0.imprint","IMPRINT",FACE,{"disambiguationData":[TD([[makeQuery(id+"F0.imprint","IMPRINT",EDGE,{"disambiguationData":[TD([[subQ9,1.0]])],"derivedFrom":subQ1}),-1.0]])]});}
            var Q3;
            Q3=makeQuery(id+"F0.imprint","IMPRINT",FACE,{"disambiguationData":[TD([[makeQuery(id+"F0.imprint","IMPRINT",EDGE,{"derivedFrom":sQuery(id+"F0.wireOp",EDGE,"E2")}),1.0]])]});
            var Q4;
            {var subQ0=sQuery(id+"F0.wireOp",EDGE,"E29");Q4=makeQuery(id+"F0.imprint","IMPRINT",FACE,{"disambiguationData":[TD([[makeQuery(id+"F0.imprint","IMPRINT",EDGE,{"derivedFrom":subQ0}),-1.0]])]});}
            var Q5;
            {var subQ0=sQuery(id+"F0.wireOp",EDGE,"E28");Q5=makeQuery(id+"F0.imprint","IMPRINT",FACE,{"disambiguationData":[TD([[makeQuery(id+"F0.imprint","IMPRINT",EDGE,{"derivedFrom":subQ0}),1.0]])]});}
            var Q6;
            {var subQ1=sQuery(id+"F0.wireOp",EDGE,"E3");var subQ9=makeQuery(id+"F0.imprint","INTERSECT",VERTEX,{"derivedFrom":[subQ1,sQuery(id+"F0.wireOp",EDGE,"E28")]});Q6=makeQuery(id+"F0.imprint","IMPRINT",FACE,{"disambiguationData":[TD([[makeQuery(id+"F0.imprint","IMPRINT",EDGE,{"disambiguationData":[TD([[subQ9,1.0]])],"derivedFrom":subQ1}),-1.0]])]});}
            var Q7;
            {var subQ0=sQuery(id+"F0.wireOp",EDGE,"E25");Q7=makeQuery(id+"F0.imprint","IMPRINT",FACE,{"disambiguationData":[TD([[makeQuery(id+"F0.imprint","IMPRINT",EDGE,{"derivedFrom":subQ0}),1.0]])]});}
            var Q8;
            {var subQ0=sQuery(id+"F0.wireOp",EDGE,"E24");Q8=makeQuery(id+"F0.imprint","IMPRINT",FACE,{"disambiguationData":[TD([[makeQuery(id+"F0.imprint","IMPRINT",EDGE,{"derivedFrom":subQ0}),-1.0]])]});}
            var Q9;
            {var subQ1=sQuery(id+"F0.wireOp",EDGE,"E3");var subQ8=makeQuery(id+"F0.imprint","INTERSECT",VERTEX,{"derivedFrom":[subQ1,sQuery(id+"F0.wireOp",EDGE,"E30")]});Q9=makeQuery(id+"F0.imprint","IMPRINT",FACE,{"disambiguationData":[TD([[makeQuery(id+"F0.imprint","IMPRINT",EDGE,{"disambiguationData":[TD([[subQ8,1.0]])],"derivedFrom":subQ1}),-1.0]])]});}
            var Q10;
            {var subQ1=sQuery(id+"F0.wireOp",EDGE,"E3");var subQ9=makeQuery(id+"F0.imprint","INTERSECT",VERTEX,{"derivedFrom":[subQ1,sQuery(id+"F0.wireOp",EDGE,"E26")]});Q10=makeQuery(id+"F0.imprint","IMPRINT",FACE,{"disambiguationData":[TD([[makeQuery(id+"F0.imprint","IMPRINT",EDGE,{"disambiguationData":[TD([[subQ9,1.0]])],"derivedFrom":subQ1}),-1.0]])]});}
            var Q11;
            {var subQ0=sQuery(id+"F0.wireOp",EDGE,"E31");Q11=makeQuery(id+"F0.imprint","IMPRINT",FACE,{"disambiguationData":[TD([[makeQuery(id+"F0.imprint","IMPRINT",EDGE,{"derivedFrom":subQ0}),-1.0]])]});}
            var Q12;
            {var subQ0=sQuery(id+"F0.wireOp",EDGE,"E30");Q12=makeQuery(id+"F0.imprint","IMPRINT",FACE,{"disambiguationData":[TD([[makeQuery(id+"F0.imprint","IMPRINT",EDGE,{"derivedFrom":subQ0}),1.0]])]});}
            var Q13;
            {var subQ6=sQuery(id+"F0.wireOp",EDGE,"E4");var subQ13=makeQuery(id+"F0.imprint","INTERSECT",VERTEX,{"derivedFrom":[subQ6,sQuery(id+"F0.wireOp",EDGE,"E30")]});Q13=makeQuery(id+"F0.imprint","IMPRINT",FACE,{"disambiguationData":[TD([[makeQuery(id+"F0.imprint","IMPRINT",EDGE,{"disambiguationData":[TD([[subQ13,1.0]])],"derivedFrom":subQ6}),1.0]])]});}
            var Q14;
            {var subQ0=sQuery(id+"F0.wireOp",EDGE,"E18.rect.top");var subQ1=sQuery(id+"F0.wireOp",EDGE,"E5");var subQ2=makeQuery(id+"F0.imprint","INTERSECT",VERTEX,{"disambiguationData":[OD(0.0)],"derivedFrom":[subQ1,subQ0]});Q14=makeQuery(id+"F0.imprint","IMPRINT",FACE,{"disambiguationData":[TD([[makeQuery(id+"F0.imprint","IMPRINT",EDGE,{"disambiguationData":[TD([[subQ2,-1.0]])],"derivedFrom":subQ1}),-1.0]])]});}
            var Q15;
            {var subQ1=sQuery(id+"F0.wireOp",EDGE,"E5");var subQ5=sQuery(id+"F0.wireOp",EDGE,"E17.rect.right");var subQ6=makeQuery(id+"F0.imprint","INTERSECT",VERTEX,{"disambiguationData":[OD(1.0)],"derivedFrom":[subQ1,subQ5]});Q15=makeQuery(id+"F0.imprint","IMPRINT",FACE,{"disambiguationData":[TD([[makeQuery(id+"F0.imprint","IMPRINT",EDGE,{"disambiguationData":[TD([[subQ6,-1.0]])],"derivedFrom":subQ1}),-1.0]])]});}
            var Q16;
            {var subQ2=sQuery(id+"F0.wireOp",EDGE,"E4");var subQ13=makeQuery(id+"F0.imprint","INTERSECT",VERTEX,{"derivedFrom":[subQ2,sQuery(id+"F0.wireOp",EDGE,"E26")]});Q16=makeQuery(id+"F0.imprint","IMPRINT",FACE,{"disambiguationData":[TD([[makeQuery(id+"F0.imprint","IMPRINT",EDGE,{"disambiguationData":[TD([[subQ13,1.0]])],"derivedFrom":subQ2}),1.0]])]});}
            var Q17;
            {var subQ0=sQuery(id+"F0.wireOp",EDGE,"E26");Q17=makeQuery(id+"F0.imprint","IMPRINT",FACE,{"disambiguationData":[TD([[makeQuery(id+"F0.imprint","IMPRINT",EDGE,{"derivedFrom":subQ0}),1.0]])]});}
            var Q18;
            {var subQ0=sQuery(id+"F0.wireOp",EDGE,"E27");Q18=makeQuery(id+"F0.imprint","IMPRINT",FACE,{"disambiguationData":[TD([[makeQuery(id+"F0.imprint","IMPRINT",EDGE,{"derivedFrom":subQ0}),-1.0]])]});}
            var Q19;
            {var subQ2=sQuery(id+"F0.wireOp",EDGE,"E4");var subQ13=makeQuery(id+"F0.imprint","INTERSECT",VERTEX,{"derivedFrom":[subQ2,sQuery(id+"F0.wireOp",EDGE,"E28")]});Q19=makeQuery(id+"F0.imprint","IMPRINT",FACE,{"disambiguationData":[TD([[makeQuery(id+"F0.imprint","IMPRINT",EDGE,{"disambiguationData":[TD([[subQ13,1.0]])],"derivedFrom":subQ2}),1.0]])]});}
            var Q20;
            {var subQ0=sQuery(id+"F0.wireOp",EDGE,"E18.rect.bottom");var subQ1=sQuery(id+"F0.wireOp",EDGE,"E5");var subQ2=makeQuery(id+"F0.imprint","INTERSECT",VERTEX,{"disambiguationData":[OD(0.0)],"derivedFrom":[subQ1,subQ0]});Q20=makeQuery(id+"F0.imprint","IMPRINT",FACE,{"disambiguationData":[TD([[makeQuery(id+"F0.imprint","IMPRINT",EDGE,{"disambiguationData":[TD([[subQ2,-1.0]])],"derivedFrom":subQ1}),-1.0]])]});}
            var Q21;
            {var subQ1=sQuery(id+"F0.wireOp",EDGE,"E5");var subQ5=sQuery(id+"F0.wireOp",EDGE,"E17.rect.left");var subQ6=makeQuery(id+"F0.imprint","INTERSECT",VERTEX,{"disambiguationData":[OD(0.0)],"derivedFrom":[subQ1,subQ5]});Q21=makeQuery(id+"F0.imprint","IMPRINT",FACE,{"disambiguationData":[TD([[makeQuery(id+"F0.imprint","IMPRINT",EDGE,{"disambiguationData":[TD([[subQ6,-1.0]])],"derivedFrom":subQ1}),-1.0]])]});}
            var Q22;
            {var subQ4=sQuery(id+"F0.wireOp",EDGE,"E4");var subQ13=makeQuery(id+"F0.imprint","INTERSECT",VERTEX,{"derivedFrom":[subQ4,sQuery(id+"F0.wireOp",EDGE,"E25")]});Q22=makeQuery(id+"F0.imprint","IMPRINT",FACE,{"disambiguationData":[TD([[makeQuery(id+"F0.imprint","IMPRINT",EDGE,{"disambiguationData":[TD([[subQ13,1.0]])],"derivedFrom":subQ4}),1.0]])]});}
            extrude(context, id + "F3", {"entities" : qUnion([Q0, Q1, Q2, Q3, Q4, Q5, Q6, Q7, Q8, Q9, Q10, Q11, Q12, Q13, Q14, Q15, Q16, Q17, Q18, Q19, Q20, Q21, Q22]), "operationType" : NewBodyOperationType.ADD, "depth" : 2 * mm});
        }
        {
            var Q0;
            {var subQ0=sQuery(id+"F0.wireOp",EDGE,"E3");var subQ1=sQuery(id+"F0.wireOp",EDGE,"c29120ee-067f-4363-a19e-8949a4685f03");Q0=makeQuery(id+"F3.boolean.opBoolean","MERGE",EDGE,{"derivedFrom":[makeQuery(id+"F2.boolean.opBoolean","MERGE",EDGE,{"derivedFrom":[makeQuery(id+"F1.opExtrude","SWEPT_EDGE",EDGE,{"disambiguationData":[OSD([subQ0,subQ1])]}),makeQuery(id+"F2.opExtrude","SWEPT_EDGE",EDGE,{"disambiguationData":[OSD([subQ0,subQ1])]})]}),makeQuery(id+"F3.opExtrude","SWEPT_EDGE",EDGE,{"disambiguationData":[OSD([subQ0,subQ1])]})]});}
            var Q1;
            {var subQ0=sQuery(id+"F0.wireOp",EDGE,"E4");var subQ1=sQuery(id+"F0.wireOp",EDGE,"c2f40e3a-2f7f-4567-aaa8-38679da907ef");Q1=makeQuery(id+"F3.boolean.opBoolean","MERGE",EDGE,{"derivedFrom":[makeQuery(id+"F2.boolean.opBoolean","MERGE",EDGE,{"derivedFrom":[makeQuery(id+"F1.opExtrude","SWEPT_EDGE",EDGE,{"disambiguationData":[OSD([subQ0,subQ1])]}),makeQuery(id+"F2.opExtrude","SWEPT_EDGE",EDGE,{"disambiguationData":[OSD([subQ0,subQ1])]})]}),makeQuery(id+"F3.opExtrude","SWEPT_EDGE",EDGE,{"disambiguationData":[OSD([subQ0,subQ1])]})]});}
            var Q2;
            {var subQ0=sQuery(id+"F0.wireOp",EDGE,"E3");var subQ1=sQuery(id+"F0.wireOp",EDGE,"ffb176a4-2236-452c-a247-1cd858443716");Q2=makeQuery(id+"F3.boolean.opBoolean","MERGE",EDGE,{"derivedFrom":[makeQuery(id+"F2.boolean.opBoolean","MERGE",EDGE,{"derivedFrom":[makeQuery(id+"F1.opExtrude","SWEPT_EDGE",EDGE,{"disambiguationData":[OSD([subQ0,subQ1])]}),makeQuery(id+"F2.opExtrude","SWEPT_EDGE",EDGE,{"disambiguationData":[OSD([subQ0,subQ1])]})]}),makeQuery(id+"F3.opExtrude","SWEPT_EDGE",EDGE,{"disambiguationData":[OSD([subQ0,subQ1])]})]});}
            var Q3;
            {var subQ0=sQuery(id+"F0.wireOp",EDGE,"E4");var subQ1=sQuery(id+"F0.wireOp",EDGE,"e9cc200f-09dc-4b27-89de-3e3ec1680f96");Q3=makeQuery(id+"F3.boolean.opBoolean","MERGE",EDGE,{"derivedFrom":[makeQuery(id+"F2.boolean.opBoolean","MERGE",EDGE,{"derivedFrom":[makeQuery(id+"F1.opExtrude","SWEPT_EDGE",EDGE,{"disambiguationData":[OSD([subQ0,subQ1])]}),makeQuery(id+"F2.opExtrude","SWEPT_EDGE",EDGE,{"disambiguationData":[OSD([subQ0,subQ1])]})]}),makeQuery(id+"F3.opExtrude","SWEPT_EDGE",EDGE,{"disambiguationData":[OSD([subQ0,subQ1])]})]});}
            var Q4;
            {var subQ0=sQuery(id+"F0.wireOp",EDGE,"E3");var subQ1=sQuery(id+"F0.wireOp",EDGE,"4b10ccc6-3fbc-4b69-a044-0f6f44fee0b3");Q4=makeQuery(id+"F3.boolean.opBoolean","MERGE",EDGE,{"derivedFrom":[makeQuery(id+"F2.boolean.opBoolean","MERGE",EDGE,{"derivedFrom":[makeQuery(id+"F1.opExtrude","SWEPT_EDGE",EDGE,{"disambiguationData":[OSD([subQ0,subQ1])]}),makeQuery(id+"F2.opExtrude","SWEPT_EDGE",EDGE,{"disambiguationData":[OSD([subQ0,subQ1])]})]}),makeQuery(id+"F3.opExtrude","SWEPT_EDGE",EDGE,{"disambiguationData":[OSD([subQ0,subQ1])]})]});}
            var Q5;
            {var subQ0=sQuery(id+"F0.wireOp",EDGE,"E3");var subQ1=sQuery(id+"F0.wireOp",EDGE,"98eb9cf6-b987-4828-be47-80f9e722f1c1");Q5=makeQuery(id+"F3.boolean.opBoolean","MERGE",EDGE,{"derivedFrom":[makeQuery(id+"F2.boolean.opBoolean","MERGE",EDGE,{"derivedFrom":[makeQuery(id+"F1.opExtrude","SWEPT_EDGE",EDGE,{"disambiguationData":[OSD([subQ0,subQ1])]}),makeQuery(id+"F2.opExtrude","SWEPT_EDGE",EDGE,{"disambiguationData":[OSD([subQ0,subQ1])]})]}),makeQuery(id+"F3.opExtrude","SWEPT_EDGE",EDGE,{"disambiguationData":[OSD([subQ0,subQ1])]})]});}
            var Q6;
            {var subQ0=sQuery(id+"F0.wireOp",EDGE,"E3");var subQ1=sQuery(id+"F0.wireOp",EDGE,"86b295ea-e671-49ad-b352-7716cfc800fb");Q6=makeQuery(id+"F3.boolean.opBoolean","MERGE",EDGE,{"derivedFrom":[makeQuery(id+"F2.boolean.opBoolean","MERGE",EDGE,{"derivedFrom":[makeQuery(id+"F1.opExtrude","SWEPT_EDGE",EDGE,{"disambiguationData":[OSD([subQ0,subQ1])]}),makeQuery(id+"F2.opExtrude","SWEPT_EDGE",EDGE,{"disambiguationData":[OSD([subQ0,subQ1])]})]}),makeQuery(id+"F3.opExtrude","SWEPT_EDGE",EDGE,{"disambiguationData":[OSD([subQ0,subQ1])]})]});}
            var Q7;
            {var subQ0=sQuery(id+"F0.wireOp",EDGE,"E4");var subQ1=sQuery(id+"F0.wireOp",EDGE,"c29120ee-067f-4363-a19e-8949a4685f03");Q7=makeQuery(id+"F3.boolean.opBoolean","MERGE",EDGE,{"derivedFrom":[makeQuery(id+"F2.boolean.opBoolean","MERGE",EDGE,{"derivedFrom":[makeQuery(id+"F1.opExtrude","SWEPT_EDGE",EDGE,{"disambiguationData":[OSD([subQ0,subQ1])]}),makeQuery(id+"F2.opExtrude","SWEPT_EDGE",EDGE,{"disambiguationData":[OSD([subQ0,subQ1])]})]}),makeQuery(id+"F3.opExtrude","SWEPT_EDGE",EDGE,{"disambiguationData":[OSD([subQ0,subQ1])]})]});}
            var Q8;
            {var subQ0=sQuery(id+"F0.wireOp",EDGE,"E3");var subQ1=sQuery(id+"F0.wireOp",EDGE,"c2f40e3a-2f7f-4567-aaa8-38679da907ef");Q8=makeQuery(id+"F3.boolean.opBoolean","MERGE",EDGE,{"derivedFrom":[makeQuery(id+"F2.boolean.opBoolean","MERGE",EDGE,{"derivedFrom":[makeQuery(id+"F1.opExtrude","SWEPT_EDGE",EDGE,{"disambiguationData":[OSD([subQ0,subQ1])]}),makeQuery(id+"F2.opExtrude","SWEPT_EDGE",EDGE,{"disambiguationData":[OSD([subQ0,subQ1])]})]}),makeQuery(id+"F3.opExtrude","SWEPT_EDGE",EDGE,{"disambiguationData":[OSD([subQ0,subQ1])]})]});}
            var Q9;
            {var subQ0=sQuery(id+"F0.wireOp",EDGE,"E4");var subQ1=sQuery(id+"F0.wireOp",EDGE,"98eb9cf6-b987-4828-be47-80f9e722f1c1");Q9=makeQuery(id+"F3.boolean.opBoolean","MERGE",EDGE,{"derivedFrom":[makeQuery(id+"F2.boolean.opBoolean","MERGE",EDGE,{"derivedFrom":[makeQuery(id+"F1.opExtrude","SWEPT_EDGE",EDGE,{"disambiguationData":[OSD([subQ0,subQ1])]}),makeQuery(id+"F2.opExtrude","SWEPT_EDGE",EDGE,{"disambiguationData":[OSD([subQ0,subQ1])]})]}),makeQuery(id+"F3.opExtrude","SWEPT_EDGE",EDGE,{"disambiguationData":[OSD([subQ0,subQ1])]})]});}
            var Q10;
            {var subQ0=sQuery(id+"F0.wireOp",EDGE,"E3");var subQ1=sQuery(id+"F0.wireOp",EDGE,"02353590-7569-472a-b830-3089a6818a80");Q10=makeQuery(id+"F3.boolean.opBoolean","MERGE",EDGE,{"derivedFrom":[makeQuery(id+"F2.boolean.opBoolean","MERGE",EDGE,{"derivedFrom":[makeQuery(id+"F1.opExtrude","SWEPT_EDGE",EDGE,{"disambiguationData":[OSD([subQ0,subQ1])]}),makeQuery(id+"F2.opExtrude","SWEPT_EDGE",EDGE,{"disambiguationData":[OSD([subQ0,subQ1])]})]}),makeQuery(id+"F3.opExtrude","SWEPT_EDGE",EDGE,{"disambiguationData":[OSD([subQ0,subQ1])]})]});}
            var Q11;
            {var subQ0=sQuery(id+"F0.wireOp",EDGE,"E3");var subQ1=sQuery(id+"F0.wireOp",EDGE,"e9cc200f-09dc-4b27-89de-3e3ec1680f96");Q11=makeQuery(id+"F3.boolean.opBoolean","MERGE",EDGE,{"derivedFrom":[makeQuery(id+"F2.boolean.opBoolean","MERGE",EDGE,{"derivedFrom":[makeQuery(id+"F1.opExtrude","SWEPT_EDGE",EDGE,{"disambiguationData":[OSD([subQ0,subQ1])]}),makeQuery(id+"F2.opExtrude","SWEPT_EDGE",EDGE,{"disambiguationData":[OSD([subQ0,subQ1])]})]}),makeQuery(id+"F3.opExtrude","SWEPT_EDGE",EDGE,{"disambiguationData":[OSD([subQ0,subQ1])]})]});}
            var Q12;
            {var subQ0=sQuery(id+"F0.wireOp",EDGE,"E4");var subQ1=sQuery(id+"F0.wireOp",EDGE,"ffb176a4-2236-452c-a247-1cd858443716");Q12=makeQuery(id+"F3.boolean.opBoolean","MERGE",EDGE,{"derivedFrom":[makeQuery(id+"F2.boolean.opBoolean","MERGE",EDGE,{"derivedFrom":[makeQuery(id+"F1.opExtrude","SWEPT_EDGE",EDGE,{"disambiguationData":[OSD([subQ0,subQ1])]}),makeQuery(id+"F2.opExtrude","SWEPT_EDGE",EDGE,{"disambiguationData":[OSD([subQ0,subQ1])]})]}),makeQuery(id+"F3.opExtrude","SWEPT_EDGE",EDGE,{"disambiguationData":[OSD([subQ0,subQ1])]})]});}
            var Q13;
            {var subQ0=sQuery(id+"F0.wireOp",EDGE,"E4");var subQ1=sQuery(id+"F0.wireOp",EDGE,"86b295ea-e671-49ad-b352-7716cfc800fb");Q13=makeQuery(id+"F3.boolean.opBoolean","MERGE",EDGE,{"derivedFrom":[makeQuery(id+"F2.boolean.opBoolean","MERGE",EDGE,{"derivedFrom":[makeQuery(id+"F1.opExtrude","SWEPT_EDGE",EDGE,{"disambiguationData":[OSD([subQ0,subQ1])]}),makeQuery(id+"F2.opExtrude","SWEPT_EDGE",EDGE,{"disambiguationData":[OSD([subQ0,subQ1])]})]}),makeQuery(id+"F3.opExtrude","SWEPT_EDGE",EDGE,{"disambiguationData":[OSD([subQ0,subQ1])]})]});}
            var Q14;
            {var subQ0=sQuery(id+"F0.wireOp",EDGE,"E4");var subQ1=sQuery(id+"F0.wireOp",EDGE,"4b10ccc6-3fbc-4b69-a044-0f6f44fee0b3");Q14=makeQuery(id+"F3.boolean.opBoolean","MERGE",EDGE,{"derivedFrom":[makeQuery(id+"F2.boolean.opBoolean","MERGE",EDGE,{"derivedFrom":[makeQuery(id+"F1.opExtrude","SWEPT_EDGE",EDGE,{"disambiguationData":[OSD([subQ0,subQ1])]}),makeQuery(id+"F2.opExtrude","SWEPT_EDGE",EDGE,{"disambiguationData":[OSD([subQ0,subQ1])]})]}),makeQuery(id+"F3.opExtrude","SWEPT_EDGE",EDGE,{"disambiguationData":[OSD([subQ0,subQ1])]})]});}
            var Q15;
            {var subQ0=sQuery(id+"F0.wireOp",EDGE,"E4");var subQ1=sQuery(id+"F0.wireOp",EDGE,"02353590-7569-472a-b830-3089a6818a80");Q15=makeQuery(id+"F3.boolean.opBoolean","MERGE",EDGE,{"derivedFrom":[makeQuery(id+"F2.boolean.opBoolean","MERGE",EDGE,{"derivedFrom":[makeQuery(id+"F1.opExtrude","SWEPT_EDGE",EDGE,{"disambiguationData":[OSD([subQ0,subQ1])]}),makeQuery(id+"F2.opExtrude","SWEPT_EDGE",EDGE,{"disambiguationData":[OSD([subQ0,subQ1])]})]}),makeQuery(id+"F3.opExtrude","SWEPT_EDGE",EDGE,{"disambiguationData":[OSD([subQ0,subQ1])]})]});}
            fillet(context, id + "F4", {"entities" : qUnion([Q0, Q1, Q2, Q3, Q4, Q5, Q6, Q7, Q8, Q9, Q10, Q11, Q12, Q13, Q14, Q15]), "radius" : 5 * mm, "tangentPropagation" : true, "allowEdgeOverflow" : false});
        }
        {
            var Q0;
            Q0=makeQuery(id+"F3.opExtrude","CAP_FACE",FACE,{"disambiguationData":[OSD([sQuery(id+"F0.wireOp",EDGE,"E2"),sQuery(id+"F0.wireOp",EDGE,"E3"),sQuery(id+"F0.wireOp",EDGE,"E4"),sQuery(id+"F0.wireOp",EDGE,"E5"),sQuery(id+"F0.wireOp",EDGE,"E6"),sQuery(id+"F0.wireOp",EDGE,"E11.rect.bottom"),sQuery(id+"F0.wireOp",EDGE,"E11.rect.top"),sQuery(id+"F0.wireOp",EDGE,"E12"),sQuery(id+"F0.wireOp",EDGE,"E13.1.0"),sQuery(id+"F0.wireOp",EDGE,"E13.2.0"),sQuery(id+"F0.wireOp",EDGE,"E13.3.0"),sQuery(id+"F0.wireOp",EDGE,"E14.rect.left"),sQuery(id+"F0.wireOp",EDGE,"E14.rect.right"),sQuery(id+"F0.wireOp",EDGE,"E17.rect.left"),sQuery(id+"F0.wireOp",EDGE,"E17.rect.right"),sQuery(id+"F0.wireOp",EDGE,"E18.rect.bottom"),sQuery(id+"F0.wireOp",EDGE,"E18.rect.top"),sQuery(id+"F0.wireOp",EDGE,"ffb176a4-2236-452c-a247-1cd858443716"),sQuery(id+"F0.wireOp",EDGE,"c29120ee-067f-4363-a19e-8949a4685f03"),sQuery(id+"F0.wireOp",EDGE,"86b295ea-e671-49ad-b352-7716cfc800fb"),sQuery(id+"F0.wireOp",EDGE,"e9cc200f-09dc-4b27-89de-3e3ec1680f96"),sQuery(id+"F0.wireOp",EDGE,"98eb9cf6-b987-4828-be47-80f9e722f1c1"),sQuery(id+"F0.wireOp",EDGE,"c2f40e3a-2f7f-4567-aaa8-38679da907ef"),sQuery(id+"F0.wireOp",EDGE,"4b10ccc6-3fbc-4b69-a044-0f6f44fee0b3"),sQuery(id+"F0.wireOp",EDGE,"02353590-7569-472a-b830-3089a6818a80")])],"isStart":false});
            var sketch = newSketch(context, id + "F5", { "sketchPlane" : qUnion([Q0])});
            skCircle(sketch, "E32", {"center": v(0, 0) * mm, "radius": 56.5 * mm});
            skCircle(sketch, "E33", {"center": v(0, 0) * mm, "radius": 97 * mm});
            skCircle(sketch, "E34", {"center": v(0, 0) * mm, "radius": 95.5 * mm});
            skLineSegment(sketch, "E35", {"start": v(0, 0) * mm, "end": v(97, 0) * mm});
            skLineSegment(sketch, "E36.1.0", {"start": v(0, 0) * mm, "end": v(68.59, 68.59) * mm});
            skLineSegment(sketch, "E36.2.0", {"start": v(0, 0) * mm, "end": v(0, 97) * mm});
            skLineSegment(sketch, "E36.3.0", {"start": v(0, 0) * mm, "end": v(-68.59, 68.59) * mm});
            skLineSegment(sketch, "E36.4.0", {"start": v(0, 0) * mm, "end": v(-97, 0) * mm});
            skLineSegment(sketch, "E36.5.0", {"start": v(0, 0) * mm, "end": v(-68.59, -68.59) * mm});
            skLineSegment(sketch, "E36.6.0", {"start": v(0, 0) * mm, "end": v(0, -97) * mm});
            skLineSegment(sketch, "E36.7.0", {"start": v(0, 0) * mm, "end": v(68.59, -68.59) * mm});
            skCircle(sketch, "E37", {"center": v(56.5, 0) * mm, "radius": 1.5 * mm});
            skCircle(sketch, "E38", {"center": v(95.5, 0) * mm, "radius": 1.5 * mm});
            skCircle(sketch, "E39", {"center": v(39.95, -39.95) * mm, "radius": 1.5 * mm});
            skCircle(sketch, "E40", {"center": v(0, -56.5) * mm, "radius": 1.5 * mm});
            skCircle(sketch, "E41", {"center": v(-39.95, -39.95) * mm, "radius": 1.5 * mm});
            skCircle(sketch, "E42", {"center": v(67.53, -67.53) * mm, "radius": 1.5 * mm});
            skCircle(sketch, "E43", {"center": v(0, -95.5) * mm, "radius": 1.5 * mm});
            skCircle(sketch, "E44", {"center": v(-67.53, -67.53) * mm, "radius": 1.5 * mm});
            skCircle(sketch, "E45", {"center": v(-56.5, 0) * mm, "radius": 1.5 * mm});
            skCircle(sketch, "E46", {"center": v(-95.5, 0) * mm, "radius": 1.5 * mm});
            skCircle(sketch, "E47", {"center": v(-39.95, 39.95) * mm, "radius": 1.5 * mm});
            skCircle(sketch, "E48", {"center": v(-67.53, 67.53) * mm, "radius": 1.5 * mm});
            skCircle(sketch, "E49", {"center": v(0, 56.5) * mm, "radius": 1.5 * mm});
            skCircle(sketch, "E50", {"center": v(39.95, 39.95) * mm, "radius": 1.5 * mm});
            skCircle(sketch, "E51", {"center": v(67.53, 67.53) * mm, "radius": 1.5 * mm});
            skCircle(sketch, "E52", {"center": v(0, 95.5) * mm, "radius": 1.5 * mm});
            skSolve(sketch);
        }
        {
            var Q0;
            Q0=sQuery(id+"F5.wireOp",VERTEX,"E45.center");
            var Q1;
            Q1=sQuery(id+"F5.wireOp",VERTEX,"E46.center");
            var Q2;
            Q2=sQuery(id+"F5.wireOp",VERTEX,"E47.center");
            var Q3;
            Q3=sQuery(id+"F5.wireOp",VERTEX,"E49.center");
            var Q4;
            Q4=sQuery(id+"F5.wireOp",VERTEX,"E50.center");
            var Q5;
            Q5=sQuery(id+"F5.wireOp",VERTEX,"E52.center");
            var Q6;
            Q6=sQuery(id+"F5.wireOp",VERTEX,"E51.center");
            var Q7;
            Q7=sQuery(id+"F5.wireOp",VERTEX,"E48.center");
            var Q8;
            Q8=sQuery(id+"F5.wireOp",VERTEX,"E38.center");
            var Q9;
            Q9=sQuery(id+"F5.wireOp",VERTEX,"E37.center");
            var Q10;
            Q10=sQuery(id+"F5.wireOp",VERTEX,"E39.center");
            var Q11;
            Q11=sQuery(id+"F5.wireOp",VERTEX,"E42.center");
            var Q12;
            Q12=sQuery(id+"F5.wireOp",VERTEX,"E40.center");
            var Q13;
            Q13=sQuery(id+"F5.wireOp",VERTEX,"E43.center");
            var Q14;
            Q14=sQuery(id+"F5.wireOp",VERTEX,"E44.center");
            var Q15;
            Q15=sQuery(id+"F5.wireOp",VERTEX,"E41.center");
            var Q16;
            Q16=makeQuery(id+"F1.opExtrude","SWEPT_BODY",BODY,{"disambiguationData":[OSD([sQuery(id+"F0.wireOp",EDGE,"E0"),sQuery(id+"F0.wireOp",EDGE,"E8")])]});
            hole(context, id + "F6", {"style" : HoleStyle.C_SINK, "holeDiameter" : 2 * mm, "cSinkDiameter" : 3 * mm, "endStyle" : HoleEndStyle.THROUGH, "locations" : qUnion([Q0, Q1, Q2, Q3, Q4, Q5, Q6, Q7, Q8, Q9, Q10, Q11, Q12, Q13, Q14, Q15]), "scope" : qUnion([Q16]), "cSinkAngle" : 90 * degree});
        }
        {
            var Q0;
            {var subQ0=sQuery(id+"F0.wireOp",EDGE,"E12");var subQ1=makeQuery(id+"F0.imprint","INTERSECT",VERTEX,{"derivedFrom":[sQuery(id+"F0.wireOp",EDGE,"E10"),subQ0]});var subQ2=sQuery(id+"F0.wireOp",EDGE,"E7");var subQ3=sQuery(id+"F0.wireOp",EDGE,"E11.rect.left");var subQ4=makeQuery(id+"F0.imprint","INTERSECT",VERTEX,{"derivedFrom":[subQ2,sQuery(id+"F0.wireOp",EDGE,"E11.rect.bottom"),subQ3,subQ0]});Q0=makeQuery(id+"F2.opExtrude","CAP_EDGE",EDGE,{"disambiguationData":[OSD([subQ0]),TDD([makeQuery(id+"F0.imprint","IMPRINT",EDGE,{"disambiguationData":[TD([[subQ1,-1.0]])],"derivedFrom":subQ0}),makeQuery(id+"F0.imprint","IMPRINT",EDGE,{"disambiguationData":[TD([[subQ4,-1.0]])],"derivedFrom":subQ0}),makeQuery(id+"F0.imprint","IMPRINT",EDGE,{"disambiguationData":[TD([[subQ1,1.0]])],"derivedFrom":subQ0})])],"isStart":false});}
            var Q1;
            {var subQ0=sQuery(id+"F0.wireOp",EDGE,"E13.1.0");var subQ1=sQuery(id+"F0.wireOp",EDGE,"E7");var subQ2=sQuery(id+"F0.wireOp",EDGE,"E14.rect.top");var subQ4=makeQuery(id+"F0.imprint","INTERSECT",VERTEX,{"derivedFrom":[subQ1,subQ0,subQ2,sQuery(id+"F0.wireOp",EDGE,"E14.rect.left")]});Q1=makeQuery(id+"F2.opExtrude","CAP_EDGE",EDGE,{"disambiguationData":[OSD([subQ0]),TDD([makeQuery(id+"F0.imprint","IMPRINT",EDGE,{"disambiguationData":[TD([[subQ4,1.0]])],"derivedFrom":subQ0}),makeQuery(id+"F0.imprint","IMPRINT",EDGE,{"disambiguationData":[TD([[subQ4,-1.0]])],"derivedFrom":subQ0})])],"isStart":false});}
            var Q2;
            {var subQ0=sQuery(id+"F0.wireOp",EDGE,"E13.2.0");var subQ1=sQuery(id+"F0.wireOp",EDGE,"E7");var subQ2=sQuery(id+"F0.wireOp",EDGE,"E11.rect.right");var subQ4=makeQuery(id+"F0.imprint","INTERSECT",VERTEX,{"derivedFrom":[subQ1,sQuery(id+"F0.wireOp",EDGE,"E11.rect.bottom"),subQ2,subQ0]});Q2=makeQuery(id+"F2.opExtrude","CAP_EDGE",EDGE,{"disambiguationData":[OSD([subQ0]),TDD([makeQuery(id+"F0.imprint","IMPRINT",EDGE,{"disambiguationData":[TD([[subQ4,1.0]])],"derivedFrom":subQ0}),makeQuery(id+"F0.imprint","IMPRINT",EDGE,{"disambiguationData":[TD([[subQ4,-1.0]])],"derivedFrom":subQ0})])],"isStart":false});}
            var Q3;
            {var subQ0=sQuery(id+"F0.wireOp",EDGE,"E13.3.0");var subQ1=sQuery(id+"F0.wireOp",EDGE,"E7");var subQ2=sQuery(id+"F0.wireOp",EDGE,"E14.rect.bottom");var subQ4=makeQuery(id+"F0.imprint","INTERSECT",VERTEX,{"derivedFrom":[subQ1,subQ0,subQ2,sQuery(id+"F0.wireOp",EDGE,"E14.rect.left")]});Q3=makeQuery(id+"F2.opExtrude","CAP_EDGE",EDGE,{"disambiguationData":[OSD([subQ0]),TDD([makeQuery(id+"F0.imprint","IMPRINT",EDGE,{"disambiguationData":[TD([[subQ4,-1.0]])],"derivedFrom":subQ0}),makeQuery(id+"F0.imprint","IMPRINT",EDGE,{"disambiguationData":[TD([[subQ4,1.0]])],"derivedFrom":subQ0})])],"isStart":false});}
            fillet(context, id + "F7", {"entities" : qUnion([Q0, Q1, Q2, Q3]), "radius" : 1 * mm, "tangentPropagation" : true, "rho" : 0.5, "crossSection" : FilletCrossSection.CONIC, "allowEdgeOverflow" : false});
        }
        {
            var Q0;
            Q0=makeQuery(id+"F3.opExtrude","CAP_EDGE",EDGE,{"disambiguationData":[OSD([sQuery(id+"F0.wireOp",EDGE,"E29")])],"isStart":false});
            var Q1;
            Q1=makeQuery(id+"F1.opExtrude","CAP_EDGE",EDGE,{"disambiguationData":[OSD([sQuery(id+"F0.wireOp",EDGE,"E29")])],"isStart":false});
            var Q2;
            {var subQ0=sQuery(id+"F0.wireOp",EDGE,"E3");var subQ1=sQuery(id+"F0.wireOp",EDGE,"E29");Q2=makeQuery(id+"F4.opFillet","BLEND_EDGE",EDGE,{"blendedFrom":[makeQuery(id+"F3.boolean.opBoolean","MERGE",EDGE,{"derivedFrom":[makeQuery(id+"F2.boolean.opBoolean","MERGE",EDGE,{"derivedFrom":[makeQuery(id+"F1.opExtrude","SWEPT_EDGE",EDGE,{"disambiguationData":[OSD([subQ0,subQ1])]}),makeQuery(id+"F2.opExtrude","SWEPT_EDGE",EDGE,{"disambiguationData":[OSD([subQ0,subQ1])]})]}),makeQuery(id+"F3.opExtrude","SWEPT_EDGE",EDGE,{"disambiguationData":[OSD([subQ0,subQ1])]})]}),makeQuery(id+"F3.opExtrude","CAP_FACE",FACE,{"disambiguationData":[OSD([sQuery(id+"F0.wireOp",EDGE,"E2"),subQ0,sQuery(id+"F0.wireOp",EDGE,"E4"),sQuery(id+"F0.wireOp",EDGE,"E5"),sQuery(id+"F0.wireOp",EDGE,"E6"),sQuery(id+"F0.wireOp",EDGE,"E11.rect.bottom"),sQuery(id+"F0.wireOp",EDGE,"E11.rect.top"),sQuery(id+"F0.wireOp",EDGE,"E12"),sQuery(id+"F0.wireOp",EDGE,"E13.1.0"),sQuery(id+"F0.wireOp",EDGE,"E13.2.0"),sQuery(id+"F0.wireOp",EDGE,"E13.3.0"),sQuery(id+"F0.wireOp",EDGE,"E14.rect.left"),sQuery(id+"F0.wireOp",EDGE,"E14.rect.right"),sQuery(id+"F0.wireOp",EDGE,"E17.rect.left"),sQuery(id+"F0.wireOp",EDGE,"E17.rect.right"),sQuery(id+"F0.wireOp",EDGE,"E18.rect.bottom"),sQuery(id+"F0.wireOp",EDGE,"E18.rect.top"),sQuery(id+"F0.wireOp",EDGE,"E24"),sQuery(id+"F0.wireOp",EDGE,"E25"),sQuery(id+"F0.wireOp",EDGE,"E26"),sQuery(id+"F0.wireOp",EDGE,"E27"),sQuery(id+"F0.wireOp",EDGE,"E28"),subQ1,sQuery(id+"F0.wireOp",EDGE,"E30"),sQuery(id+"F0.wireOp",EDGE,"E31")])],"isStart":false})],"blendedInto":[makeQuery(id+"F3.opExtrude","CAP_FACE",FACE,{"disambiguationData":[OSD([sQuery(id+"F0.wireOp",EDGE,"E2"),subQ0,sQuery(id+"F0.wireOp",EDGE,"E4"),sQuery(id+"F0.wireOp",EDGE,"E5"),sQuery(id+"F0.wireOp",EDGE,"E6"),sQuery(id+"F0.wireOp",EDGE,"E11.rect.bottom"),sQuery(id+"F0.wireOp",EDGE,"E11.rect.top"),sQuery(id+"F0.wireOp",EDGE,"E12"),sQuery(id+"F0.wireOp",EDGE,"E13.1.0"),sQuery(id+"F0.wireOp",EDGE,"E13.2.0"),sQuery(id+"F0.wireOp",EDGE,"E13.3.0"),sQuery(id+"F0.wireOp",EDGE,"E14.rect.left"),sQuery(id+"F0.wireOp",EDGE,"E14.rect.right"),sQuery(id+"F0.wireOp",EDGE,"E17.rect.left"),sQuery(id+"F0.wireOp",EDGE,"E17.rect.right"),sQuery(id+"F0.wireOp",EDGE,"E18.rect.bottom"),sQuery(id+"F0.wireOp",EDGE,"E18.rect.top"),sQuery(id+"F0.wireOp",EDGE,"E24"),sQuery(id+"F0.wireOp",EDGE,"E25"),sQuery(id+"F0.wireOp",EDGE,"E26"),sQuery(id+"F0.wireOp",EDGE,"E27"),sQuery(id+"F0.wireOp",EDGE,"E28"),subQ1,sQuery(id+"F0.wireOp",EDGE,"E30"),sQuery(id+"F0.wireOp",EDGE,"E31")])],"isStart":false})]});}
            var Q3;
            {var subQ0=sQuery(id+"F0.wireOp",EDGE,"E3");var subQ1=sQuery(id+"F0.wireOp",EDGE,"E29");Q3=makeQuery(id+"F4.opFillet","BLEND_EDGE",EDGE,{"blendedFrom":[makeQuery(id+"F3.boolean.opBoolean","MERGE",EDGE,{"derivedFrom":[makeQuery(id+"F2.boolean.opBoolean","MERGE",EDGE,{"derivedFrom":[makeQuery(id+"F1.opExtrude","SWEPT_EDGE",EDGE,{"disambiguationData":[OSD([subQ0,subQ1])]}),makeQuery(id+"F2.opExtrude","SWEPT_EDGE",EDGE,{"disambiguationData":[OSD([subQ0,subQ1])]})]}),makeQuery(id+"F3.opExtrude","SWEPT_EDGE",EDGE,{"disambiguationData":[OSD([subQ0,subQ1])]})]}),makeQuery(id+"F1.opExtrude","CAP_FACE",FACE,{"disambiguationData":[OSD([sQuery(id+"F0.wireOp",EDGE,"E2"),subQ0,sQuery(id+"F0.wireOp",EDGE,"E4"),sQuery(id+"F0.wireOp",EDGE,"E5"),sQuery(id+"F0.wireOp",EDGE,"E6"),sQuery(id+"F0.wireOp",EDGE,"E11.rect.bottom"),sQuery(id+"F0.wireOp",EDGE,"E11.rect.top"),sQuery(id+"F0.wireOp",EDGE,"E12"),sQuery(id+"F0.wireOp",EDGE,"E13.1.0"),sQuery(id+"F0.wireOp",EDGE,"E13.2.0"),sQuery(id+"F0.wireOp",EDGE,"E13.3.0"),sQuery(id+"F0.wireOp",EDGE,"E14.rect.left"),sQuery(id+"F0.wireOp",EDGE,"E14.rect.right"),sQuery(id+"F0.wireOp",EDGE,"E17.rect.left"),sQuery(id+"F0.wireOp",EDGE,"E17.rect.right"),sQuery(id+"F0.wireOp",EDGE,"E18.rect.bottom"),sQuery(id+"F0.wireOp",EDGE,"E18.rect.top"),sQuery(id+"F0.wireOp",EDGE,"E19"),sQuery(id+"F0.wireOp",EDGE,"E20"),sQuery(id+"F0.wireOp",EDGE,"E21"),sQuery(id+"F0.wireOp",EDGE,"E22"),sQuery(id+"F0.wireOp",EDGE,"E24"),sQuery(id+"F0.wireOp",EDGE,"E25"),sQuery(id+"F0.wireOp",EDGE,"E26"),sQuery(id+"F0.wireOp",EDGE,"E27"),sQuery(id+"F0.wireOp",EDGE,"E28"),subQ1,sQuery(id+"F0.wireOp",EDGE,"E30"),sQuery(id+"F0.wireOp",EDGE,"E31")])],"isStart":false})],"blendedInto":[makeQuery(id+"F1.opExtrude","CAP_FACE",FACE,{"disambiguationData":[OSD([sQuery(id+"F0.wireOp",EDGE,"E2"),subQ0,sQuery(id+"F0.wireOp",EDGE,"E4"),sQuery(id+"F0.wireOp",EDGE,"E5"),sQuery(id+"F0.wireOp",EDGE,"E6"),sQuery(id+"F0.wireOp",EDGE,"E11.rect.bottom"),sQuery(id+"F0.wireOp",EDGE,"E11.rect.top"),sQuery(id+"F0.wireOp",EDGE,"E12"),sQuery(id+"F0.wireOp",EDGE,"E13.1.0"),sQuery(id+"F0.wireOp",EDGE,"E13.2.0"),sQuery(id+"F0.wireOp",EDGE,"E13.3.0"),sQuery(id+"F0.wireOp",EDGE,"E14.rect.left"),sQuery(id+"F0.wireOp",EDGE,"E14.rect.right"),sQuery(id+"F0.wireOp",EDGE,"E17.rect.left"),sQuery(id+"F0.wireOp",EDGE,"E17.rect.right"),sQuery(id+"F0.wireOp",EDGE,"E18.rect.bottom"),sQuery(id+"F0.wireOp",EDGE,"E18.rect.top"),sQuery(id+"F0.wireOp",EDGE,"E19"),sQuery(id+"F0.wireOp",EDGE,"E20"),sQuery(id+"F0.wireOp",EDGE,"E21"),sQuery(id+"F0.wireOp",EDGE,"E22"),sQuery(id+"F0.wireOp",EDGE,"E24"),sQuery(id+"F0.wireOp",EDGE,"E25"),sQuery(id+"F0.wireOp",EDGE,"E26"),sQuery(id+"F0.wireOp",EDGE,"E27"),sQuery(id+"F0.wireOp",EDGE,"E28"),subQ1,sQuery(id+"F0.wireOp",EDGE,"E30"),sQuery(id+"F0.wireOp",EDGE,"E31")])],"isStart":false})]});}
            var Q4;
            {var subQ0=sQuery(id+"F0.wireOp",EDGE,"E3");Q4=makeQuery(id+"F3.opExtrude","CAP_EDGE",EDGE,{"disambiguationData":[OSD([subQ0]),TDD([makeQuery(id+"F0.imprint","IMPRINT",EDGE,{"disambiguationData":[TD([[makeQuery(id+"F0.imprint","INTERSECT",VERTEX,{"derivedFrom":[subQ0,sQuery(id+"F0.wireOp",EDGE,"E25")]}),-1.0]])],"derivedFrom":subQ0})])],"isStart":false});}
            var Q5;
            {var subQ0=sQuery(id+"F0.wireOp",EDGE,"E4");var subQ1=sQuery(id+"F0.wireOp",EDGE,"E29");Q5=makeQuery(id+"F4.opFillet","BLEND_EDGE",EDGE,{"blendedFrom":[makeQuery(id+"F3.boolean.opBoolean","MERGE",EDGE,{"derivedFrom":[makeQuery(id+"F2.boolean.opBoolean","MERGE",EDGE,{"derivedFrom":[makeQuery(id+"F1.opExtrude","SWEPT_EDGE",EDGE,{"disambiguationData":[OSD([subQ0,subQ1])]}),makeQuery(id+"F2.opExtrude","SWEPT_EDGE",EDGE,{"disambiguationData":[OSD([subQ0,subQ1])]})]}),makeQuery(id+"F3.opExtrude","SWEPT_EDGE",EDGE,{"disambiguationData":[OSD([subQ0,subQ1])]})]}),makeQuery(id+"F3.opExtrude","CAP_FACE",FACE,{"disambiguationData":[OSD([sQuery(id+"F0.wireOp",EDGE,"E2"),sQuery(id+"F0.wireOp",EDGE,"E3"),subQ0,sQuery(id+"F0.wireOp",EDGE,"E5"),sQuery(id+"F0.wireOp",EDGE,"E6"),sQuery(id+"F0.wireOp",EDGE,"E11.rect.bottom"),sQuery(id+"F0.wireOp",EDGE,"E11.rect.top"),sQuery(id+"F0.wireOp",EDGE,"E12"),sQuery(id+"F0.wireOp",EDGE,"E13.1.0"),sQuery(id+"F0.wireOp",EDGE,"E13.2.0"),sQuery(id+"F0.wireOp",EDGE,"E13.3.0"),sQuery(id+"F0.wireOp",EDGE,"E14.rect.left"),sQuery(id+"F0.wireOp",EDGE,"E14.rect.right"),sQuery(id+"F0.wireOp",EDGE,"E17.rect.left"),sQuery(id+"F0.wireOp",EDGE,"E17.rect.right"),sQuery(id+"F0.wireOp",EDGE,"E18.rect.bottom"),sQuery(id+"F0.wireOp",EDGE,"E18.rect.top"),sQuery(id+"F0.wireOp",EDGE,"E24"),sQuery(id+"F0.wireOp",EDGE,"E25"),sQuery(id+"F0.wireOp",EDGE,"E26"),sQuery(id+"F0.wireOp",EDGE,"E27"),sQuery(id+"F0.wireOp",EDGE,"E28"),subQ1,sQuery(id+"F0.wireOp",EDGE,"E30"),sQuery(id+"F0.wireOp",EDGE,"E31")])],"isStart":false})],"blendedInto":[makeQuery(id+"F3.opExtrude","CAP_FACE",FACE,{"disambiguationData":[OSD([sQuery(id+"F0.wireOp",EDGE,"E2"),sQuery(id+"F0.wireOp",EDGE,"E3"),subQ0,sQuery(id+"F0.wireOp",EDGE,"E5"),sQuery(id+"F0.wireOp",EDGE,"E6"),sQuery(id+"F0.wireOp",EDGE,"E11.rect.bottom"),sQuery(id+"F0.wireOp",EDGE,"E11.rect.top"),sQuery(id+"F0.wireOp",EDGE,"E12"),sQuery(id+"F0.wireOp",EDGE,"E13.1.0"),sQuery(id+"F0.wireOp",EDGE,"E13.2.0"),sQuery(id+"F0.wireOp",EDGE,"E13.3.0"),sQuery(id+"F0.wireOp",EDGE,"E14.rect.left"),sQuery(id+"F0.wireOp",EDGE,"E14.rect.right"),sQuery(id+"F0.wireOp",EDGE,"E17.rect.left"),sQuery(id+"F0.wireOp",EDGE,"E17.rect.right"),sQuery(id+"F0.wireOp",EDGE,"E18.rect.bottom"),sQuery(id+"F0.wireOp",EDGE,"E18.rect.top"),sQuery(id+"F0.wireOp",EDGE,"E24"),sQuery(id+"F0.wireOp",EDGE,"E25"),sQuery(id+"F0.wireOp",EDGE,"E26"),sQuery(id+"F0.wireOp",EDGE,"E27"),sQuery(id+"F0.wireOp",EDGE,"E28"),subQ1,sQuery(id+"F0.wireOp",EDGE,"E30"),sQuery(id+"F0.wireOp",EDGE,"E31")])],"isStart":false})]});}
            var Q6;
            {var subQ0=sQuery(id+"F0.wireOp",EDGE,"E4");var subQ1=sQuery(id+"F0.wireOp",EDGE,"E29");Q6=makeQuery(id+"F4.opFillet","BLEND_EDGE",EDGE,{"blendedFrom":[makeQuery(id+"F3.boolean.opBoolean","MERGE",EDGE,{"derivedFrom":[makeQuery(id+"F2.boolean.opBoolean","MERGE",EDGE,{"derivedFrom":[makeQuery(id+"F1.opExtrude","SWEPT_EDGE",EDGE,{"disambiguationData":[OSD([subQ0,subQ1])]}),makeQuery(id+"F2.opExtrude","SWEPT_EDGE",EDGE,{"disambiguationData":[OSD([subQ0,subQ1])]})]}),makeQuery(id+"F3.opExtrude","SWEPT_EDGE",EDGE,{"disambiguationData":[OSD([subQ0,subQ1])]})]}),makeQuery(id+"F1.opExtrude","CAP_FACE",FACE,{"disambiguationData":[OSD([sQuery(id+"F0.wireOp",EDGE,"E2"),sQuery(id+"F0.wireOp",EDGE,"E3"),subQ0,sQuery(id+"F0.wireOp",EDGE,"E5"),sQuery(id+"F0.wireOp",EDGE,"E6"),sQuery(id+"F0.wireOp",EDGE,"E11.rect.bottom"),sQuery(id+"F0.wireOp",EDGE,"E11.rect.top"),sQuery(id+"F0.wireOp",EDGE,"E12"),sQuery(id+"F0.wireOp",EDGE,"E13.1.0"),sQuery(id+"F0.wireOp",EDGE,"E13.2.0"),sQuery(id+"F0.wireOp",EDGE,"E13.3.0"),sQuery(id+"F0.wireOp",EDGE,"E14.rect.left"),sQuery(id+"F0.wireOp",EDGE,"E14.rect.right"),sQuery(id+"F0.wireOp",EDGE,"E17.rect.left"),sQuery(id+"F0.wireOp",EDGE,"E17.rect.right"),sQuery(id+"F0.wireOp",EDGE,"E18.rect.bottom"),sQuery(id+"F0.wireOp",EDGE,"E18.rect.top"),sQuery(id+"F0.wireOp",EDGE,"E19"),sQuery(id+"F0.wireOp",EDGE,"E20"),sQuery(id+"F0.wireOp",EDGE,"E21"),sQuery(id+"F0.wireOp",EDGE,"E22"),sQuery(id+"F0.wireOp",EDGE,"E24"),sQuery(id+"F0.wireOp",EDGE,"E25"),sQuery(id+"F0.wireOp",EDGE,"E26"),sQuery(id+"F0.wireOp",EDGE,"E27"),sQuery(id+"F0.wireOp",EDGE,"E28"),subQ1,sQuery(id+"F0.wireOp",EDGE,"E30"),sQuery(id+"F0.wireOp",EDGE,"E31")])],"isStart":false})],"blendedInto":[makeQuery(id+"F1.opExtrude","CAP_FACE",FACE,{"disambiguationData":[OSD([sQuery(id+"F0.wireOp",EDGE,"E2"),sQuery(id+"F0.wireOp",EDGE,"E3"),subQ0,sQuery(id+"F0.wireOp",EDGE,"E5"),sQuery(id+"F0.wireOp",EDGE,"E6"),sQuery(id+"F0.wireOp",EDGE,"E11.rect.bottom"),sQuery(id+"F0.wireOp",EDGE,"E11.rect.top"),sQuery(id+"F0.wireOp",EDGE,"E12"),sQuery(id+"F0.wireOp",EDGE,"E13.1.0"),sQuery(id+"F0.wireOp",EDGE,"E13.2.0"),sQuery(id+"F0.wireOp",EDGE,"E13.3.0"),sQuery(id+"F0.wireOp",EDGE,"E14.rect.left"),sQuery(id+"F0.wireOp",EDGE,"E14.rect.right"),sQuery(id+"F0.wireOp",EDGE,"E17.rect.left"),sQuery(id+"F0.wireOp",EDGE,"E17.rect.right"),sQuery(id+"F0.wireOp",EDGE,"E18.rect.bottom"),sQuery(id+"F0.wireOp",EDGE,"E18.rect.top"),sQuery(id+"F0.wireOp",EDGE,"E19"),sQuery(id+"F0.wireOp",EDGE,"E20"),sQuery(id+"F0.wireOp",EDGE,"E21"),sQuery(id+"F0.wireOp",EDGE,"E22"),sQuery(id+"F0.wireOp",EDGE,"E24"),sQuery(id+"F0.wireOp",EDGE,"E25"),sQuery(id+"F0.wireOp",EDGE,"E26"),sQuery(id+"F0.wireOp",EDGE,"E27"),sQuery(id+"F0.wireOp",EDGE,"E28"),subQ1,sQuery(id+"F0.wireOp",EDGE,"E30"),sQuery(id+"F0.wireOp",EDGE,"E31")])],"isStart":false})]});}
            var Q7;
            {var subQ0=sQuery(id+"F0.wireOp",EDGE,"E4");Q7=makeQuery(id+"F3.opExtrude","CAP_EDGE",EDGE,{"disambiguationData":[OSD([subQ0]),TDD([makeQuery(id+"F0.imprint","IMPRINT",EDGE,{"disambiguationData":[TD([[makeQuery(id+"F0.imprint","INTERSECT",VERTEX,{"derivedFrom":[subQ0,sQuery(id+"F0.wireOp",EDGE,"E25")]}),-1.0]])],"derivedFrom":subQ0})])],"isStart":false});}
            var Q8;
            {var subQ0=sQuery(id+"F0.wireOp",EDGE,"E4");Q8=makeQuery(id+"F1.opExtrude","CAP_EDGE",EDGE,{"disambiguationData":[OSD([subQ0]),TDD([makeQuery(id+"F0.imprint","IMPRINT",EDGE,{"disambiguationData":[TD([[makeQuery(id+"F0.imprint","INTERSECT",VERTEX,{"derivedFrom":[subQ0,sQuery(id+"F0.wireOp",EDGE,"E25")]}),-1.0]])],"derivedFrom":subQ0})])],"isStart":false});}
            var Q9;
            {var subQ0=sQuery(id+"F0.wireOp",EDGE,"E4");var subQ1=sQuery(id+"F0.wireOp",EDGE,"E25");Q9=makeQuery(id+"F4.opFillet","BLEND_EDGE",EDGE,{"blendedFrom":[makeQuery(id+"F3.boolean.opBoolean","MERGE",EDGE,{"derivedFrom":[makeQuery(id+"F2.boolean.opBoolean","MERGE",EDGE,{"derivedFrom":[makeQuery(id+"F1.opExtrude","SWEPT_EDGE",EDGE,{"disambiguationData":[OSD([subQ0,subQ1])]}),makeQuery(id+"F2.opExtrude","SWEPT_EDGE",EDGE,{"disambiguationData":[OSD([subQ0,subQ1])]})]}),makeQuery(id+"F3.opExtrude","SWEPT_EDGE",EDGE,{"disambiguationData":[OSD([subQ0,subQ1])]})]}),makeQuery(id+"F3.opExtrude","CAP_FACE",FACE,{"disambiguationData":[OSD([sQuery(id+"F0.wireOp",EDGE,"E2"),sQuery(id+"F0.wireOp",EDGE,"E3"),subQ0,sQuery(id+"F0.wireOp",EDGE,"E5"),sQuery(id+"F0.wireOp",EDGE,"E6"),sQuery(id+"F0.wireOp",EDGE,"E11.rect.bottom"),sQuery(id+"F0.wireOp",EDGE,"E11.rect.top"),sQuery(id+"F0.wireOp",EDGE,"E12"),sQuery(id+"F0.wireOp",EDGE,"E13.1.0"),sQuery(id+"F0.wireOp",EDGE,"E13.2.0"),sQuery(id+"F0.wireOp",EDGE,"E13.3.0"),sQuery(id+"F0.wireOp",EDGE,"E14.rect.left"),sQuery(id+"F0.wireOp",EDGE,"E14.rect.right"),sQuery(id+"F0.wireOp",EDGE,"E17.rect.left"),sQuery(id+"F0.wireOp",EDGE,"E17.rect.right"),sQuery(id+"F0.wireOp",EDGE,"E18.rect.bottom"),sQuery(id+"F0.wireOp",EDGE,"E18.rect.top"),sQuery(id+"F0.wireOp",EDGE,"E24"),subQ1,sQuery(id+"F0.wireOp",EDGE,"E26"),sQuery(id+"F0.wireOp",EDGE,"E27"),sQuery(id+"F0.wireOp",EDGE,"E28"),sQuery(id+"F0.wireOp",EDGE,"E29"),sQuery(id+"F0.wireOp",EDGE,"E30"),sQuery(id+"F0.wireOp",EDGE,"E31")])],"isStart":false})],"blendedInto":[makeQuery(id+"F3.opExtrude","CAP_FACE",FACE,{"disambiguationData":[OSD([sQuery(id+"F0.wireOp",EDGE,"E2"),sQuery(id+"F0.wireOp",EDGE,"E3"),subQ0,sQuery(id+"F0.wireOp",EDGE,"E5"),sQuery(id+"F0.wireOp",EDGE,"E6"),sQuery(id+"F0.wireOp",EDGE,"E11.rect.bottom"),sQuery(id+"F0.wireOp",EDGE,"E11.rect.top"),sQuery(id+"F0.wireOp",EDGE,"E12"),sQuery(id+"F0.wireOp",EDGE,"E13.1.0"),sQuery(id+"F0.wireOp",EDGE,"E13.2.0"),sQuery(id+"F0.wireOp",EDGE,"E13.3.0"),sQuery(id+"F0.wireOp",EDGE,"E14.rect.left"),sQuery(id+"F0.wireOp",EDGE,"E14.rect.right"),sQuery(id+"F0.wireOp",EDGE,"E17.rect.left"),sQuery(id+"F0.wireOp",EDGE,"E17.rect.right"),sQuery(id+"F0.wireOp",EDGE,"E18.rect.bottom"),sQuery(id+"F0.wireOp",EDGE,"E18.rect.top"),sQuery(id+"F0.wireOp",EDGE,"E24"),subQ1,sQuery(id+"F0.wireOp",EDGE,"E26"),sQuery(id+"F0.wireOp",EDGE,"E27"),sQuery(id+"F0.wireOp",EDGE,"E28"),sQuery(id+"F0.wireOp",EDGE,"E29"),sQuery(id+"F0.wireOp",EDGE,"E30"),sQuery(id+"F0.wireOp",EDGE,"E31")])],"isStart":false})]});}
            var Q10;
            {var subQ0=sQuery(id+"F0.wireOp",EDGE,"E4");var subQ1=sQuery(id+"F0.wireOp",EDGE,"E25");Q10=makeQuery(id+"F4.opFillet","BLEND_EDGE",EDGE,{"blendedFrom":[makeQuery(id+"F3.boolean.opBoolean","MERGE",EDGE,{"derivedFrom":[makeQuery(id+"F2.boolean.opBoolean","MERGE",EDGE,{"derivedFrom":[makeQuery(id+"F1.opExtrude","SWEPT_EDGE",EDGE,{"disambiguationData":[OSD([subQ0,subQ1])]}),makeQuery(id+"F2.opExtrude","SWEPT_EDGE",EDGE,{"disambiguationData":[OSD([subQ0,subQ1])]})]}),makeQuery(id+"F3.opExtrude","SWEPT_EDGE",EDGE,{"disambiguationData":[OSD([subQ0,subQ1])]})]}),makeQuery(id+"F1.opExtrude","CAP_FACE",FACE,{"disambiguationData":[OSD([sQuery(id+"F0.wireOp",EDGE,"E2"),sQuery(id+"F0.wireOp",EDGE,"E3"),subQ0,sQuery(id+"F0.wireOp",EDGE,"E5"),sQuery(id+"F0.wireOp",EDGE,"E6"),sQuery(id+"F0.wireOp",EDGE,"E11.rect.bottom"),sQuery(id+"F0.wireOp",EDGE,"E11.rect.top"),sQuery(id+"F0.wireOp",EDGE,"E12"),sQuery(id+"F0.wireOp",EDGE,"E13.1.0"),sQuery(id+"F0.wireOp",EDGE,"E13.2.0"),sQuery(id+"F0.wireOp",EDGE,"E13.3.0"),sQuery(id+"F0.wireOp",EDGE,"E14.rect.left"),sQuery(id+"F0.wireOp",EDGE,"E14.rect.right"),sQuery(id+"F0.wireOp",EDGE,"E17.rect.left"),sQuery(id+"F0.wireOp",EDGE,"E17.rect.right"),sQuery(id+"F0.wireOp",EDGE,"E18.rect.bottom"),sQuery(id+"F0.wireOp",EDGE,"E18.rect.top"),sQuery(id+"F0.wireOp",EDGE,"E19"),sQuery(id+"F0.wireOp",EDGE,"E20"),sQuery(id+"F0.wireOp",EDGE,"E21"),sQuery(id+"F0.wireOp",EDGE,"E22"),sQuery(id+"F0.wireOp",EDGE,"E24"),subQ1,sQuery(id+"F0.wireOp",EDGE,"E26"),sQuery(id+"F0.wireOp",EDGE,"E27"),sQuery(id+"F0.wireOp",EDGE,"E28"),sQuery(id+"F0.wireOp",EDGE,"E29"),sQuery(id+"F0.wireOp",EDGE,"E30"),sQuery(id+"F0.wireOp",EDGE,"E31")])],"isStart":false})],"blendedInto":[makeQuery(id+"F1.opExtrude","CAP_FACE",FACE,{"disambiguationData":[OSD([sQuery(id+"F0.wireOp",EDGE,"E2"),sQuery(id+"F0.wireOp",EDGE,"E3"),subQ0,sQuery(id+"F0.wireOp",EDGE,"E5"),sQuery(id+"F0.wireOp",EDGE,"E6"),sQuery(id+"F0.wireOp",EDGE,"E11.rect.bottom"),sQuery(id+"F0.wireOp",EDGE,"E11.rect.top"),sQuery(id+"F0.wireOp",EDGE,"E12"),sQuery(id+"F0.wireOp",EDGE,"E13.1.0"),sQuery(id+"F0.wireOp",EDGE,"E13.2.0"),sQuery(id+"F0.wireOp",EDGE,"E13.3.0"),sQuery(id+"F0.wireOp",EDGE,"E14.rect.left"),sQuery(id+"F0.wireOp",EDGE,"E14.rect.right"),sQuery(id+"F0.wireOp",EDGE,"E17.rect.left"),sQuery(id+"F0.wireOp",EDGE,"E17.rect.right"),sQuery(id+"F0.wireOp",EDGE,"E18.rect.bottom"),sQuery(id+"F0.wireOp",EDGE,"E18.rect.top"),sQuery(id+"F0.wireOp",EDGE,"E19"),sQuery(id+"F0.wireOp",EDGE,"E20"),sQuery(id+"F0.wireOp",EDGE,"E21"),sQuery(id+"F0.wireOp",EDGE,"E22"),sQuery(id+"F0.wireOp",EDGE,"E24"),subQ1,sQuery(id+"F0.wireOp",EDGE,"E26"),sQuery(id+"F0.wireOp",EDGE,"E27"),sQuery(id+"F0.wireOp",EDGE,"E28"),sQuery(id+"F0.wireOp",EDGE,"E29"),sQuery(id+"F0.wireOp",EDGE,"E30"),sQuery(id+"F0.wireOp",EDGE,"E31")])],"isStart":false})]});}
            var Q11;
            Q11=makeQuery(id+"F3.opExtrude","CAP_EDGE",EDGE,{"disambiguationData":[OSD([sQuery(id+"F0.wireOp",EDGE,"E25")])],"isStart":false});
            var Q12;
            {var subQ0=sQuery(id+"F0.wireOp",EDGE,"E3");var subQ1=sQuery(id+"F0.wireOp",EDGE,"E25");Q12=makeQuery(id+"F4.opFillet","BLEND_EDGE",EDGE,{"blendedFrom":[makeQuery(id+"F3.boolean.opBoolean","MERGE",EDGE,{"derivedFrom":[makeQuery(id+"F2.boolean.opBoolean","MERGE",EDGE,{"derivedFrom":[makeQuery(id+"F1.opExtrude","SWEPT_EDGE",EDGE,{"disambiguationData":[OSD([subQ0,subQ1])]}),makeQuery(id+"F2.opExtrude","SWEPT_EDGE",EDGE,{"disambiguationData":[OSD([subQ0,subQ1])]})]}),makeQuery(id+"F3.opExtrude","SWEPT_EDGE",EDGE,{"disambiguationData":[OSD([subQ0,subQ1])]})]}),makeQuery(id+"F3.opExtrude","CAP_FACE",FACE,{"disambiguationData":[OSD([sQuery(id+"F0.wireOp",EDGE,"E2"),subQ0,sQuery(id+"F0.wireOp",EDGE,"E4"),sQuery(id+"F0.wireOp",EDGE,"E5"),sQuery(id+"F0.wireOp",EDGE,"E6"),sQuery(id+"F0.wireOp",EDGE,"E11.rect.bottom"),sQuery(id+"F0.wireOp",EDGE,"E11.rect.top"),sQuery(id+"F0.wireOp",EDGE,"E12"),sQuery(id+"F0.wireOp",EDGE,"E13.1.0"),sQuery(id+"F0.wireOp",EDGE,"E13.2.0"),sQuery(id+"F0.wireOp",EDGE,"E13.3.0"),sQuery(id+"F0.wireOp",EDGE,"E14.rect.left"),sQuery(id+"F0.wireOp",EDGE,"E14.rect.right"),sQuery(id+"F0.wireOp",EDGE,"E17.rect.left"),sQuery(id+"F0.wireOp",EDGE,"E17.rect.right"),sQuery(id+"F0.wireOp",EDGE,"E18.rect.bottom"),sQuery(id+"F0.wireOp",EDGE,"E18.rect.top"),sQuery(id+"F0.wireOp",EDGE,"E24"),subQ1,sQuery(id+"F0.wireOp",EDGE,"E26"),sQuery(id+"F0.wireOp",EDGE,"E27"),sQuery(id+"F0.wireOp",EDGE,"E28"),sQuery(id+"F0.wireOp",EDGE,"E29"),sQuery(id+"F0.wireOp",EDGE,"E30"),sQuery(id+"F0.wireOp",EDGE,"E31")])],"isStart":false})],"blendedInto":[makeQuery(id+"F3.opExtrude","CAP_FACE",FACE,{"disambiguationData":[OSD([sQuery(id+"F0.wireOp",EDGE,"E2"),subQ0,sQuery(id+"F0.wireOp",EDGE,"E4"),sQuery(id+"F0.wireOp",EDGE,"E5"),sQuery(id+"F0.wireOp",EDGE,"E6"),sQuery(id+"F0.wireOp",EDGE,"E11.rect.bottom"),sQuery(id+"F0.wireOp",EDGE,"E11.rect.top"),sQuery(id+"F0.wireOp",EDGE,"E12"),sQuery(id+"F0.wireOp",EDGE,"E13.1.0"),sQuery(id+"F0.wireOp",EDGE,"E13.2.0"),sQuery(id+"F0.wireOp",EDGE,"E13.3.0"),sQuery(id+"F0.wireOp",EDGE,"E14.rect.left"),sQuery(id+"F0.wireOp",EDGE,"E14.rect.right"),sQuery(id+"F0.wireOp",EDGE,"E17.rect.left"),sQuery(id+"F0.wireOp",EDGE,"E17.rect.right"),sQuery(id+"F0.wireOp",EDGE,"E18.rect.bottom"),sQuery(id+"F0.wireOp",EDGE,"E18.rect.top"),sQuery(id+"F0.wireOp",EDGE,"E24"),subQ1,sQuery(id+"F0.wireOp",EDGE,"E26"),sQuery(id+"F0.wireOp",EDGE,"E27"),sQuery(id+"F0.wireOp",EDGE,"E28"),sQuery(id+"F0.wireOp",EDGE,"E29"),sQuery(id+"F0.wireOp",EDGE,"E30"),sQuery(id+"F0.wireOp",EDGE,"E31")])],"isStart":false})]});}
            var Q13;
            Q13=makeQuery(id+"F1.opExtrude","CAP_EDGE",EDGE,{"disambiguationData":[OSD([sQuery(id+"F0.wireOp",EDGE,"E25")])],"isStart":false});
            var Q14;
            {var subQ0=sQuery(id+"F0.wireOp",EDGE,"E3");var subQ1=sQuery(id+"F0.wireOp",EDGE,"E25");Q14=makeQuery(id+"F4.opFillet","BLEND_EDGE",EDGE,{"blendedFrom":[makeQuery(id+"F3.boolean.opBoolean","MERGE",EDGE,{"derivedFrom":[makeQuery(id+"F2.boolean.opBoolean","MERGE",EDGE,{"derivedFrom":[makeQuery(id+"F1.opExtrude","SWEPT_EDGE",EDGE,{"disambiguationData":[OSD([subQ0,subQ1])]}),makeQuery(id+"F2.opExtrude","SWEPT_EDGE",EDGE,{"disambiguationData":[OSD([subQ0,subQ1])]})]}),makeQuery(id+"F3.opExtrude","SWEPT_EDGE",EDGE,{"disambiguationData":[OSD([subQ0,subQ1])]})]}),makeQuery(id+"F1.opExtrude","CAP_FACE",FACE,{"disambiguationData":[OSD([sQuery(id+"F0.wireOp",EDGE,"E2"),subQ0,sQuery(id+"F0.wireOp",EDGE,"E4"),sQuery(id+"F0.wireOp",EDGE,"E5"),sQuery(id+"F0.wireOp",EDGE,"E6"),sQuery(id+"F0.wireOp",EDGE,"E11.rect.bottom"),sQuery(id+"F0.wireOp",EDGE,"E11.rect.top"),sQuery(id+"F0.wireOp",EDGE,"E12"),sQuery(id+"F0.wireOp",EDGE,"E13.1.0"),sQuery(id+"F0.wireOp",EDGE,"E13.2.0"),sQuery(id+"F0.wireOp",EDGE,"E13.3.0"),sQuery(id+"F0.wireOp",EDGE,"E14.rect.left"),sQuery(id+"F0.wireOp",EDGE,"E14.rect.right"),sQuery(id+"F0.wireOp",EDGE,"E17.rect.left"),sQuery(id+"F0.wireOp",EDGE,"E17.rect.right"),sQuery(id+"F0.wireOp",EDGE,"E18.rect.bottom"),sQuery(id+"F0.wireOp",EDGE,"E18.rect.top"),sQuery(id+"F0.wireOp",EDGE,"E19"),sQuery(id+"F0.wireOp",EDGE,"E20"),sQuery(id+"F0.wireOp",EDGE,"E21"),sQuery(id+"F0.wireOp",EDGE,"E22"),sQuery(id+"F0.wireOp",EDGE,"E24"),subQ1,sQuery(id+"F0.wireOp",EDGE,"E26"),sQuery(id+"F0.wireOp",EDGE,"E27"),sQuery(id+"F0.wireOp",EDGE,"E28"),sQuery(id+"F0.wireOp",EDGE,"E29"),sQuery(id+"F0.wireOp",EDGE,"E30"),sQuery(id+"F0.wireOp",EDGE,"E31")])],"isStart":false})],"blendedInto":[makeQuery(id+"F1.opExtrude","CAP_FACE",FACE,{"disambiguationData":[OSD([sQuery(id+"F0.wireOp",EDGE,"E2"),subQ0,sQuery(id+"F0.wireOp",EDGE,"E4"),sQuery(id+"F0.wireOp",EDGE,"E5"),sQuery(id+"F0.wireOp",EDGE,"E6"),sQuery(id+"F0.wireOp",EDGE,"E11.rect.bottom"),sQuery(id+"F0.wireOp",EDGE,"E11.rect.top"),sQuery(id+"F0.wireOp",EDGE,"E12"),sQuery(id+"F0.wireOp",EDGE,"E13.1.0"),sQuery(id+"F0.wireOp",EDGE,"E13.2.0"),sQuery(id+"F0.wireOp",EDGE,"E13.3.0"),sQuery(id+"F0.wireOp",EDGE,"E14.rect.left"),sQuery(id+"F0.wireOp",EDGE,"E14.rect.right"),sQuery(id+"F0.wireOp",EDGE,"E17.rect.left"),sQuery(id+"F0.wireOp",EDGE,"E17.rect.right"),sQuery(id+"F0.wireOp",EDGE,"E18.rect.bottom"),sQuery(id+"F0.wireOp",EDGE,"E18.rect.top"),sQuery(id+"F0.wireOp",EDGE,"E19"),sQuery(id+"F0.wireOp",EDGE,"E20"),sQuery(id+"F0.wireOp",EDGE,"E21"),sQuery(id+"F0.wireOp",EDGE,"E22"),sQuery(id+"F0.wireOp",EDGE,"E24"),subQ1,sQuery(id+"F0.wireOp",EDGE,"E26"),sQuery(id+"F0.wireOp",EDGE,"E27"),sQuery(id+"F0.wireOp",EDGE,"E28"),sQuery(id+"F0.wireOp",EDGE,"E29"),sQuery(id+"F0.wireOp",EDGE,"E30"),sQuery(id+"F0.wireOp",EDGE,"E31")])],"isStart":false})]});}
            var Q15;
            {var subQ0=sQuery(id+"F0.wireOp",EDGE,"E3");Q15=makeQuery(id+"F1.opExtrude","CAP_EDGE",EDGE,{"disambiguationData":[OSD([subQ0]),TDD([makeQuery(id+"F0.imprint","IMPRINT",EDGE,{"disambiguationData":[TD([[makeQuery(id+"F0.imprint","INTERSECT",VERTEX,{"derivedFrom":[subQ0,sQuery(id+"F0.wireOp",EDGE,"E25")]}),-1.0]])],"derivedFrom":subQ0})])],"isStart":false});}
            var Q16;
            Q16=makeQuery(id+"F1.opExtrude","CAP_EDGE",EDGE,{"disambiguationData":[OSD([sQuery(id+"F0.wireOp",EDGE,"E24")])],"isStart":false});
            var Q17;
            Q17=makeQuery(id+"F3.opExtrude","CAP_EDGE",EDGE,{"disambiguationData":[OSD([sQuery(id+"F0.wireOp",EDGE,"E24")])],"isStart":false});
            var Q18;
            {var subQ0=sQuery(id+"F0.wireOp",EDGE,"E3");var subQ1=sQuery(id+"F0.wireOp",EDGE,"E24");Q18=makeQuery(id+"F4.opFillet","BLEND_EDGE",EDGE,{"blendedFrom":[makeQuery(id+"F3.boolean.opBoolean","MERGE",EDGE,{"derivedFrom":[makeQuery(id+"F2.boolean.opBoolean","MERGE",EDGE,{"derivedFrom":[makeQuery(id+"F1.opExtrude","SWEPT_EDGE",EDGE,{"disambiguationData":[OSD([subQ0,subQ1])]}),makeQuery(id+"F2.opExtrude","SWEPT_EDGE",EDGE,{"disambiguationData":[OSD([subQ0,subQ1])]})]}),makeQuery(id+"F3.opExtrude","SWEPT_EDGE",EDGE,{"disambiguationData":[OSD([subQ0,subQ1])]})]}),makeQuery(id+"F1.opExtrude","CAP_FACE",FACE,{"disambiguationData":[OSD([sQuery(id+"F0.wireOp",EDGE,"E2"),subQ0,sQuery(id+"F0.wireOp",EDGE,"E4"),sQuery(id+"F0.wireOp",EDGE,"E5"),sQuery(id+"F0.wireOp",EDGE,"E6"),sQuery(id+"F0.wireOp",EDGE,"E11.rect.bottom"),sQuery(id+"F0.wireOp",EDGE,"E11.rect.top"),sQuery(id+"F0.wireOp",EDGE,"E12"),sQuery(id+"F0.wireOp",EDGE,"E13.1.0"),sQuery(id+"F0.wireOp",EDGE,"E13.2.0"),sQuery(id+"F0.wireOp",EDGE,"E13.3.0"),sQuery(id+"F0.wireOp",EDGE,"E14.rect.left"),sQuery(id+"F0.wireOp",EDGE,"E14.rect.right"),sQuery(id+"F0.wireOp",EDGE,"E17.rect.left"),sQuery(id+"F0.wireOp",EDGE,"E17.rect.right"),sQuery(id+"F0.wireOp",EDGE,"E18.rect.bottom"),sQuery(id+"F0.wireOp",EDGE,"E18.rect.top"),sQuery(id+"F0.wireOp",EDGE,"E19"),sQuery(id+"F0.wireOp",EDGE,"E20"),sQuery(id+"F0.wireOp",EDGE,"E21"),sQuery(id+"F0.wireOp",EDGE,"E22"),subQ1,sQuery(id+"F0.wireOp",EDGE,"E25"),sQuery(id+"F0.wireOp",EDGE,"E26"),sQuery(id+"F0.wireOp",EDGE,"E27"),sQuery(id+"F0.wireOp",EDGE,"E28"),sQuery(id+"F0.wireOp",EDGE,"E29"),sQuery(id+"F0.wireOp",EDGE,"E30"),sQuery(id+"F0.wireOp",EDGE,"E31")])],"isStart":false})],"blendedInto":[makeQuery(id+"F1.opExtrude","CAP_FACE",FACE,{"disambiguationData":[OSD([sQuery(id+"F0.wireOp",EDGE,"E2"),subQ0,sQuery(id+"F0.wireOp",EDGE,"E4"),sQuery(id+"F0.wireOp",EDGE,"E5"),sQuery(id+"F0.wireOp",EDGE,"E6"),sQuery(id+"F0.wireOp",EDGE,"E11.rect.bottom"),sQuery(id+"F0.wireOp",EDGE,"E11.rect.top"),sQuery(id+"F0.wireOp",EDGE,"E12"),sQuery(id+"F0.wireOp",EDGE,"E13.1.0"),sQuery(id+"F0.wireOp",EDGE,"E13.2.0"),sQuery(id+"F0.wireOp",EDGE,"E13.3.0"),sQuery(id+"F0.wireOp",EDGE,"E14.rect.left"),sQuery(id+"F0.wireOp",EDGE,"E14.rect.right"),sQuery(id+"F0.wireOp",EDGE,"E17.rect.left"),sQuery(id+"F0.wireOp",EDGE,"E17.rect.right"),sQuery(id+"F0.wireOp",EDGE,"E18.rect.bottom"),sQuery(id+"F0.wireOp",EDGE,"E18.rect.top"),sQuery(id+"F0.wireOp",EDGE,"E19"),sQuery(id+"F0.wireOp",EDGE,"E20"),sQuery(id+"F0.wireOp",EDGE,"E21"),sQuery(id+"F0.wireOp",EDGE,"E22"),subQ1,sQuery(id+"F0.wireOp",EDGE,"E25"),sQuery(id+"F0.wireOp",EDGE,"E26"),sQuery(id+"F0.wireOp",EDGE,"E27"),sQuery(id+"F0.wireOp",EDGE,"E28"),sQuery(id+"F0.wireOp",EDGE,"E29"),sQuery(id+"F0.wireOp",EDGE,"E30"),sQuery(id+"F0.wireOp",EDGE,"E31")])],"isStart":false})]});}
            var Q19;
            {var subQ0=sQuery(id+"F0.wireOp",EDGE,"E3");var subQ1=sQuery(id+"F0.wireOp",EDGE,"E24");Q19=makeQuery(id+"F4.opFillet","BLEND_EDGE",EDGE,{"blendedFrom":[makeQuery(id+"F3.boolean.opBoolean","MERGE",EDGE,{"derivedFrom":[makeQuery(id+"F2.boolean.opBoolean","MERGE",EDGE,{"derivedFrom":[makeQuery(id+"F1.opExtrude","SWEPT_EDGE",EDGE,{"disambiguationData":[OSD([subQ0,subQ1])]}),makeQuery(id+"F2.opExtrude","SWEPT_EDGE",EDGE,{"disambiguationData":[OSD([subQ0,subQ1])]})]}),makeQuery(id+"F3.opExtrude","SWEPT_EDGE",EDGE,{"disambiguationData":[OSD([subQ0,subQ1])]})]}),makeQuery(id+"F3.opExtrude","CAP_FACE",FACE,{"disambiguationData":[OSD([sQuery(id+"F0.wireOp",EDGE,"E2"),subQ0,sQuery(id+"F0.wireOp",EDGE,"E4"),sQuery(id+"F0.wireOp",EDGE,"E5"),sQuery(id+"F0.wireOp",EDGE,"E6"),sQuery(id+"F0.wireOp",EDGE,"E11.rect.bottom"),sQuery(id+"F0.wireOp",EDGE,"E11.rect.top"),sQuery(id+"F0.wireOp",EDGE,"E12"),sQuery(id+"F0.wireOp",EDGE,"E13.1.0"),sQuery(id+"F0.wireOp",EDGE,"E13.2.0"),sQuery(id+"F0.wireOp",EDGE,"E13.3.0"),sQuery(id+"F0.wireOp",EDGE,"E14.rect.left"),sQuery(id+"F0.wireOp",EDGE,"E14.rect.right"),sQuery(id+"F0.wireOp",EDGE,"E17.rect.left"),sQuery(id+"F0.wireOp",EDGE,"E17.rect.right"),sQuery(id+"F0.wireOp",EDGE,"E18.rect.bottom"),sQuery(id+"F0.wireOp",EDGE,"E18.rect.top"),subQ1,sQuery(id+"F0.wireOp",EDGE,"E25"),sQuery(id+"F0.wireOp",EDGE,"E26"),sQuery(id+"F0.wireOp",EDGE,"E27"),sQuery(id+"F0.wireOp",EDGE,"E28"),sQuery(id+"F0.wireOp",EDGE,"E29"),sQuery(id+"F0.wireOp",EDGE,"E30"),sQuery(id+"F0.wireOp",EDGE,"E31")])],"isStart":false})],"blendedInto":[makeQuery(id+"F3.opExtrude","CAP_FACE",FACE,{"disambiguationData":[OSD([sQuery(id+"F0.wireOp",EDGE,"E2"),subQ0,sQuery(id+"F0.wireOp",EDGE,"E4"),sQuery(id+"F0.wireOp",EDGE,"E5"),sQuery(id+"F0.wireOp",EDGE,"E6"),sQuery(id+"F0.wireOp",EDGE,"E11.rect.bottom"),sQuery(id+"F0.wireOp",EDGE,"E11.rect.top"),sQuery(id+"F0.wireOp",EDGE,"E12"),sQuery(id+"F0.wireOp",EDGE,"E13.1.0"),sQuery(id+"F0.wireOp",EDGE,"E13.2.0"),sQuery(id+"F0.wireOp",EDGE,"E13.3.0"),sQuery(id+"F0.wireOp",EDGE,"E14.rect.left"),sQuery(id+"F0.wireOp",EDGE,"E14.rect.right"),sQuery(id+"F0.wireOp",EDGE,"E17.rect.left"),sQuery(id+"F0.wireOp",EDGE,"E17.rect.right"),sQuery(id+"F0.wireOp",EDGE,"E18.rect.bottom"),sQuery(id+"F0.wireOp",EDGE,"E18.rect.top"),subQ1,sQuery(id+"F0.wireOp",EDGE,"E25"),sQuery(id+"F0.wireOp",EDGE,"E26"),sQuery(id+"F0.wireOp",EDGE,"E27"),sQuery(id+"F0.wireOp",EDGE,"E28"),sQuery(id+"F0.wireOp",EDGE,"E29"),sQuery(id+"F0.wireOp",EDGE,"E30"),sQuery(id+"F0.wireOp",EDGE,"E31")])],"isStart":false})]});}
            var Q20;
            Q20=makeQuery(id+"F3.opExtrude","CAP_EDGE",EDGE,{"disambiguationData":[OSD([sQuery(id+"F0.wireOp",EDGE,"E28")])],"isStart":false});
            var Q21;
            {var subQ0=sQuery(id+"F0.wireOp",EDGE,"E3");var subQ1=sQuery(id+"F0.wireOp",EDGE,"E28");Q21=makeQuery(id+"F4.opFillet","BLEND_EDGE",EDGE,{"blendedFrom":[makeQuery(id+"F3.boolean.opBoolean","MERGE",EDGE,{"derivedFrom":[makeQuery(id+"F2.boolean.opBoolean","MERGE",EDGE,{"derivedFrom":[makeQuery(id+"F1.opExtrude","SWEPT_EDGE",EDGE,{"disambiguationData":[OSD([subQ0,subQ1])]}),makeQuery(id+"F2.opExtrude","SWEPT_EDGE",EDGE,{"disambiguationData":[OSD([subQ0,subQ1])]})]}),makeQuery(id+"F3.opExtrude","SWEPT_EDGE",EDGE,{"disambiguationData":[OSD([subQ0,subQ1])]})]}),makeQuery(id+"F1.opExtrude","CAP_FACE",FACE,{"disambiguationData":[OSD([sQuery(id+"F0.wireOp",EDGE,"E2"),subQ0,sQuery(id+"F0.wireOp",EDGE,"E4"),sQuery(id+"F0.wireOp",EDGE,"E5"),sQuery(id+"F0.wireOp",EDGE,"E6"),sQuery(id+"F0.wireOp",EDGE,"E11.rect.bottom"),sQuery(id+"F0.wireOp",EDGE,"E11.rect.top"),sQuery(id+"F0.wireOp",EDGE,"E12"),sQuery(id+"F0.wireOp",EDGE,"E13.1.0"),sQuery(id+"F0.wireOp",EDGE,"E13.2.0"),sQuery(id+"F0.wireOp",EDGE,"E13.3.0"),sQuery(id+"F0.wireOp",EDGE,"E14.rect.left"),sQuery(id+"F0.wireOp",EDGE,"E14.rect.right"),sQuery(id+"F0.wireOp",EDGE,"E17.rect.left"),sQuery(id+"F0.wireOp",EDGE,"E17.rect.right"),sQuery(id+"F0.wireOp",EDGE,"E18.rect.bottom"),sQuery(id+"F0.wireOp",EDGE,"E18.rect.top"),sQuery(id+"F0.wireOp",EDGE,"E19"),sQuery(id+"F0.wireOp",EDGE,"E20"),sQuery(id+"F0.wireOp",EDGE,"E21"),sQuery(id+"F0.wireOp",EDGE,"E22"),sQuery(id+"F0.wireOp",EDGE,"E24"),sQuery(id+"F0.wireOp",EDGE,"E25"),sQuery(id+"F0.wireOp",EDGE,"E26"),sQuery(id+"F0.wireOp",EDGE,"E27"),subQ1,sQuery(id+"F0.wireOp",EDGE,"E29"),sQuery(id+"F0.wireOp",EDGE,"E30"),sQuery(id+"F0.wireOp",EDGE,"E31")])],"isStart":false})],"blendedInto":[makeQuery(id+"F1.opExtrude","CAP_FACE",FACE,{"disambiguationData":[OSD([sQuery(id+"F0.wireOp",EDGE,"E2"),subQ0,sQuery(id+"F0.wireOp",EDGE,"E4"),sQuery(id+"F0.wireOp",EDGE,"E5"),sQuery(id+"F0.wireOp",EDGE,"E6"),sQuery(id+"F0.wireOp",EDGE,"E11.rect.bottom"),sQuery(id+"F0.wireOp",EDGE,"E11.rect.top"),sQuery(id+"F0.wireOp",EDGE,"E12"),sQuery(id+"F0.wireOp",EDGE,"E13.1.0"),sQuery(id+"F0.wireOp",EDGE,"E13.2.0"),sQuery(id+"F0.wireOp",EDGE,"E13.3.0"),sQuery(id+"F0.wireOp",EDGE,"E14.rect.left"),sQuery(id+"F0.wireOp",EDGE,"E14.rect.right"),sQuery(id+"F0.wireOp",EDGE,"E17.rect.left"),sQuery(id+"F0.wireOp",EDGE,"E17.rect.right"),sQuery(id+"F0.wireOp",EDGE,"E18.rect.bottom"),sQuery(id+"F0.wireOp",EDGE,"E18.rect.top"),sQuery(id+"F0.wireOp",EDGE,"E19"),sQuery(id+"F0.wireOp",EDGE,"E20"),sQuery(id+"F0.wireOp",EDGE,"E21"),sQuery(id+"F0.wireOp",EDGE,"E22"),sQuery(id+"F0.wireOp",EDGE,"E24"),sQuery(id+"F0.wireOp",EDGE,"E25"),sQuery(id+"F0.wireOp",EDGE,"E26"),sQuery(id+"F0.wireOp",EDGE,"E27"),subQ1,sQuery(id+"F0.wireOp",EDGE,"E29"),sQuery(id+"F0.wireOp",EDGE,"E30"),sQuery(id+"F0.wireOp",EDGE,"E31")])],"isStart":false})]});}
            var Q22;
            {var subQ0=sQuery(id+"F0.wireOp",EDGE,"E3");Q22=makeQuery(id+"F1.opExtrude","CAP_EDGE",EDGE,{"disambiguationData":[OSD([subQ0]),TDD([makeQuery(id+"F0.imprint","IMPRINT",EDGE,{"disambiguationData":[TD([[makeQuery(id+"F0.imprint","INTERSECT",VERTEX,{"derivedFrom":[subQ0,sQuery(id+"F0.wireOp",EDGE,"E27")]}),1.0]])],"derivedFrom":subQ0})])],"isStart":false});}
            var Q23;
            Q23=makeQuery(id+"F1.opExtrude","CAP_EDGE",EDGE,{"disambiguationData":[OSD([sQuery(id+"F0.wireOp",EDGE,"E26")])],"isStart":false});
            var Q24;
            {var subQ0=sQuery(id+"F0.wireOp",EDGE,"E3");var subQ1=sQuery(id+"F0.wireOp",EDGE,"E31");Q24=makeQuery(id+"F4.opFillet","BLEND_EDGE",EDGE,{"blendedFrom":[makeQuery(id+"F3.boolean.opBoolean","MERGE",EDGE,{"derivedFrom":[makeQuery(id+"F2.boolean.opBoolean","MERGE",EDGE,{"derivedFrom":[makeQuery(id+"F1.opExtrude","SWEPT_EDGE",EDGE,{"disambiguationData":[OSD([subQ0,subQ1])]}),makeQuery(id+"F2.opExtrude","SWEPT_EDGE",EDGE,{"disambiguationData":[OSD([subQ0,subQ1])]})]}),makeQuery(id+"F3.opExtrude","SWEPT_EDGE",EDGE,{"disambiguationData":[OSD([subQ0,subQ1])]})]}),makeQuery(id+"F3.opExtrude","CAP_FACE",FACE,{"disambiguationData":[OSD([sQuery(id+"F0.wireOp",EDGE,"E2"),subQ0,sQuery(id+"F0.wireOp",EDGE,"E4"),sQuery(id+"F0.wireOp",EDGE,"E5"),sQuery(id+"F0.wireOp",EDGE,"E6"),sQuery(id+"F0.wireOp",EDGE,"E11.rect.bottom"),sQuery(id+"F0.wireOp",EDGE,"E11.rect.top"),sQuery(id+"F0.wireOp",EDGE,"E12"),sQuery(id+"F0.wireOp",EDGE,"E13.1.0"),sQuery(id+"F0.wireOp",EDGE,"E13.2.0"),sQuery(id+"F0.wireOp",EDGE,"E13.3.0"),sQuery(id+"F0.wireOp",EDGE,"E14.rect.left"),sQuery(id+"F0.wireOp",EDGE,"E14.rect.right"),sQuery(id+"F0.wireOp",EDGE,"E17.rect.left"),sQuery(id+"F0.wireOp",EDGE,"E17.rect.right"),sQuery(id+"F0.wireOp",EDGE,"E18.rect.bottom"),sQuery(id+"F0.wireOp",EDGE,"E18.rect.top"),sQuery(id+"F0.wireOp",EDGE,"E24"),sQuery(id+"F0.wireOp",EDGE,"E25"),sQuery(id+"F0.wireOp",EDGE,"E26"),sQuery(id+"F0.wireOp",EDGE,"E27"),sQuery(id+"F0.wireOp",EDGE,"E28"),sQuery(id+"F0.wireOp",EDGE,"E29"),sQuery(id+"F0.wireOp",EDGE,"E30"),subQ1])],"isStart":false})],"blendedInto":[makeQuery(id+"F3.opExtrude","CAP_FACE",FACE,{"disambiguationData":[OSD([sQuery(id+"F0.wireOp",EDGE,"E2"),subQ0,sQuery(id+"F0.wireOp",EDGE,"E4"),sQuery(id+"F0.wireOp",EDGE,"E5"),sQuery(id+"F0.wireOp",EDGE,"E6"),sQuery(id+"F0.wireOp",EDGE,"E11.rect.bottom"),sQuery(id+"F0.wireOp",EDGE,"E11.rect.top"),sQuery(id+"F0.wireOp",EDGE,"E12"),sQuery(id+"F0.wireOp",EDGE,"E13.1.0"),sQuery(id+"F0.wireOp",EDGE,"E13.2.0"),sQuery(id+"F0.wireOp",EDGE,"E13.3.0"),sQuery(id+"F0.wireOp",EDGE,"E14.rect.left"),sQuery(id+"F0.wireOp",EDGE,"E14.rect.right"),sQuery(id+"F0.wireOp",EDGE,"E17.rect.left"),sQuery(id+"F0.wireOp",EDGE,"E17.rect.right"),sQuery(id+"F0.wireOp",EDGE,"E18.rect.bottom"),sQuery(id+"F0.wireOp",EDGE,"E18.rect.top"),sQuery(id+"F0.wireOp",EDGE,"E24"),sQuery(id+"F0.wireOp",EDGE,"E25"),sQuery(id+"F0.wireOp",EDGE,"E26"),sQuery(id+"F0.wireOp",EDGE,"E27"),sQuery(id+"F0.wireOp",EDGE,"E28"),sQuery(id+"F0.wireOp",EDGE,"E29"),sQuery(id+"F0.wireOp",EDGE,"E30"),subQ1])],"isStart":false})]});}
            var Q25;
            Q25=makeQuery(id+"F3.opExtrude","CAP_EDGE",EDGE,{"disambiguationData":[OSD([sQuery(id+"F0.wireOp",EDGE,"E31")])],"isStart":false});
            var Q26;
            {var subQ0=sQuery(id+"F0.wireOp",EDGE,"E4");var subQ1=sQuery(id+"F0.wireOp",EDGE,"E31");Q26=makeQuery(id+"F4.opFillet","BLEND_EDGE",EDGE,{"blendedFrom":[makeQuery(id+"F3.boolean.opBoolean","MERGE",EDGE,{"derivedFrom":[makeQuery(id+"F2.boolean.opBoolean","MERGE",EDGE,{"derivedFrom":[makeQuery(id+"F1.opExtrude","SWEPT_EDGE",EDGE,{"disambiguationData":[OSD([subQ0,subQ1])]}),makeQuery(id+"F2.opExtrude","SWEPT_EDGE",EDGE,{"disambiguationData":[OSD([subQ0,subQ1])]})]}),makeQuery(id+"F3.opExtrude","SWEPT_EDGE",EDGE,{"disambiguationData":[OSD([subQ0,subQ1])]})]}),makeQuery(id+"F3.opExtrude","CAP_FACE",FACE,{"disambiguationData":[OSD([sQuery(id+"F0.wireOp",EDGE,"E2"),sQuery(id+"F0.wireOp",EDGE,"E3"),subQ0,sQuery(id+"F0.wireOp",EDGE,"E5"),sQuery(id+"F0.wireOp",EDGE,"E6"),sQuery(id+"F0.wireOp",EDGE,"E11.rect.bottom"),sQuery(id+"F0.wireOp",EDGE,"E11.rect.top"),sQuery(id+"F0.wireOp",EDGE,"E12"),sQuery(id+"F0.wireOp",EDGE,"E13.1.0"),sQuery(id+"F0.wireOp",EDGE,"E13.2.0"),sQuery(id+"F0.wireOp",EDGE,"E13.3.0"),sQuery(id+"F0.wireOp",EDGE,"E14.rect.left"),sQuery(id+"F0.wireOp",EDGE,"E14.rect.right"),sQuery(id+"F0.wireOp",EDGE,"E17.rect.left"),sQuery(id+"F0.wireOp",EDGE,"E17.rect.right"),sQuery(id+"F0.wireOp",EDGE,"E18.rect.bottom"),sQuery(id+"F0.wireOp",EDGE,"E18.rect.top"),sQuery(id+"F0.wireOp",EDGE,"E24"),sQuery(id+"F0.wireOp",EDGE,"E25"),sQuery(id+"F0.wireOp",EDGE,"E26"),sQuery(id+"F0.wireOp",EDGE,"E27"),sQuery(id+"F0.wireOp",EDGE,"E28"),sQuery(id+"F0.wireOp",EDGE,"E29"),sQuery(id+"F0.wireOp",EDGE,"E30"),subQ1])],"isStart":false})],"blendedInto":[makeQuery(id+"F3.opExtrude","CAP_FACE",FACE,{"disambiguationData":[OSD([sQuery(id+"F0.wireOp",EDGE,"E2"),sQuery(id+"F0.wireOp",EDGE,"E3"),subQ0,sQuery(id+"F0.wireOp",EDGE,"E5"),sQuery(id+"F0.wireOp",EDGE,"E6"),sQuery(id+"F0.wireOp",EDGE,"E11.rect.bottom"),sQuery(id+"F0.wireOp",EDGE,"E11.rect.top"),sQuery(id+"F0.wireOp",EDGE,"E12"),sQuery(id+"F0.wireOp",EDGE,"E13.1.0"),sQuery(id+"F0.wireOp",EDGE,"E13.2.0"),sQuery(id+"F0.wireOp",EDGE,"E13.3.0"),sQuery(id+"F0.wireOp",EDGE,"E14.rect.left"),sQuery(id+"F0.wireOp",EDGE,"E14.rect.right"),sQuery(id+"F0.wireOp",EDGE,"E17.rect.left"),sQuery(id+"F0.wireOp",EDGE,"E17.rect.right"),sQuery(id+"F0.wireOp",EDGE,"E18.rect.bottom"),sQuery(id+"F0.wireOp",EDGE,"E18.rect.top"),sQuery(id+"F0.wireOp",EDGE,"E24"),sQuery(id+"F0.wireOp",EDGE,"E25"),sQuery(id+"F0.wireOp",EDGE,"E26"),sQuery(id+"F0.wireOp",EDGE,"E27"),sQuery(id+"F0.wireOp",EDGE,"E28"),sQuery(id+"F0.wireOp",EDGE,"E29"),sQuery(id+"F0.wireOp",EDGE,"E30"),subQ1])],"isStart":false})]});}
            var Q27;
            {var subQ0=sQuery(id+"F0.wireOp",EDGE,"E4");Q27=makeQuery(id+"F3.opExtrude","CAP_EDGE",EDGE,{"disambiguationData":[OSD([subQ0]),TDD([makeQuery(id+"F0.imprint","IMPRINT",EDGE,{"disambiguationData":[TD([[makeQuery(id+"F0.imprint","INTERSECT",VERTEX,{"derivedFrom":[subQ0,sQuery(id+"F0.wireOp",EDGE,"E26")]}),-1.0]])],"derivedFrom":subQ0})])],"isStart":false});}
            var Q28;
            {var subQ0=sQuery(id+"F0.wireOp",EDGE,"E4");var subQ1=sQuery(id+"F0.wireOp",EDGE,"E26");Q28=makeQuery(id+"F4.opFillet","BLEND_EDGE",EDGE,{"blendedFrom":[makeQuery(id+"F3.boolean.opBoolean","MERGE",EDGE,{"derivedFrom":[makeQuery(id+"F2.boolean.opBoolean","MERGE",EDGE,{"derivedFrom":[makeQuery(id+"F1.opExtrude","SWEPT_EDGE",EDGE,{"disambiguationData":[OSD([subQ0,subQ1])]}),makeQuery(id+"F2.opExtrude","SWEPT_EDGE",EDGE,{"disambiguationData":[OSD([subQ0,subQ1])]})]}),makeQuery(id+"F3.opExtrude","SWEPT_EDGE",EDGE,{"disambiguationData":[OSD([subQ0,subQ1])]})]}),makeQuery(id+"F3.opExtrude","CAP_FACE",FACE,{"disambiguationData":[OSD([sQuery(id+"F0.wireOp",EDGE,"E2"),sQuery(id+"F0.wireOp",EDGE,"E3"),subQ0,sQuery(id+"F0.wireOp",EDGE,"E5"),sQuery(id+"F0.wireOp",EDGE,"E6"),sQuery(id+"F0.wireOp",EDGE,"E11.rect.bottom"),sQuery(id+"F0.wireOp",EDGE,"E11.rect.top"),sQuery(id+"F0.wireOp",EDGE,"E12"),sQuery(id+"F0.wireOp",EDGE,"E13.1.0"),sQuery(id+"F0.wireOp",EDGE,"E13.2.0"),sQuery(id+"F0.wireOp",EDGE,"E13.3.0"),sQuery(id+"F0.wireOp",EDGE,"E14.rect.left"),sQuery(id+"F0.wireOp",EDGE,"E14.rect.right"),sQuery(id+"F0.wireOp",EDGE,"E17.rect.left"),sQuery(id+"F0.wireOp",EDGE,"E17.rect.right"),sQuery(id+"F0.wireOp",EDGE,"E18.rect.bottom"),sQuery(id+"F0.wireOp",EDGE,"E18.rect.top"),sQuery(id+"F0.wireOp",EDGE,"E24"),sQuery(id+"F0.wireOp",EDGE,"E25"),subQ1,sQuery(id+"F0.wireOp",EDGE,"E27"),sQuery(id+"F0.wireOp",EDGE,"E28"),sQuery(id+"F0.wireOp",EDGE,"E29"),sQuery(id+"F0.wireOp",EDGE,"E30"),sQuery(id+"F0.wireOp",EDGE,"E31")])],"isStart":false})],"blendedInto":[makeQuery(id+"F3.opExtrude","CAP_FACE",FACE,{"disambiguationData":[OSD([sQuery(id+"F0.wireOp",EDGE,"E2"),sQuery(id+"F0.wireOp",EDGE,"E3"),subQ0,sQuery(id+"F0.wireOp",EDGE,"E5"),sQuery(id+"F0.wireOp",EDGE,"E6"),sQuery(id+"F0.wireOp",EDGE,"E11.rect.bottom"),sQuery(id+"F0.wireOp",EDGE,"E11.rect.top"),sQuery(id+"F0.wireOp",EDGE,"E12"),sQuery(id+"F0.wireOp",EDGE,"E13.1.0"),sQuery(id+"F0.wireOp",EDGE,"E13.2.0"),sQuery(id+"F0.wireOp",EDGE,"E13.3.0"),sQuery(id+"F0.wireOp",EDGE,"E14.rect.left"),sQuery(id+"F0.wireOp",EDGE,"E14.rect.right"),sQuery(id+"F0.wireOp",EDGE,"E17.rect.left"),sQuery(id+"F0.wireOp",EDGE,"E17.rect.right"),sQuery(id+"F0.wireOp",EDGE,"E18.rect.bottom"),sQuery(id+"F0.wireOp",EDGE,"E18.rect.top"),sQuery(id+"F0.wireOp",EDGE,"E24"),sQuery(id+"F0.wireOp",EDGE,"E25"),subQ1,sQuery(id+"F0.wireOp",EDGE,"E27"),sQuery(id+"F0.wireOp",EDGE,"E28"),sQuery(id+"F0.wireOp",EDGE,"E29"),sQuery(id+"F0.wireOp",EDGE,"E30"),sQuery(id+"F0.wireOp",EDGE,"E31")])],"isStart":false})]});}
            var Q29;
            Q29=makeQuery(id+"F3.opExtrude","CAP_EDGE",EDGE,{"disambiguationData":[OSD([sQuery(id+"F0.wireOp",EDGE,"E26")])],"isStart":false});
            fillet(context, id + "F8", {"entities" : qUnion([Q0, Q1, Q2, Q3, Q4, Q5, Q6, Q7, Q8, Q9, Q10, Q11, Q12, Q13, Q14, Q15, Q16, Q17, Q18, Q19, Q20, Q21, Q22, Q23, Q24, Q25, Q26, Q27, Q28, Q29]), "radius" : 1.5 * mm, "tangentPropagation" : true, "allowEdgeOverflow" : false});
        }
    });
